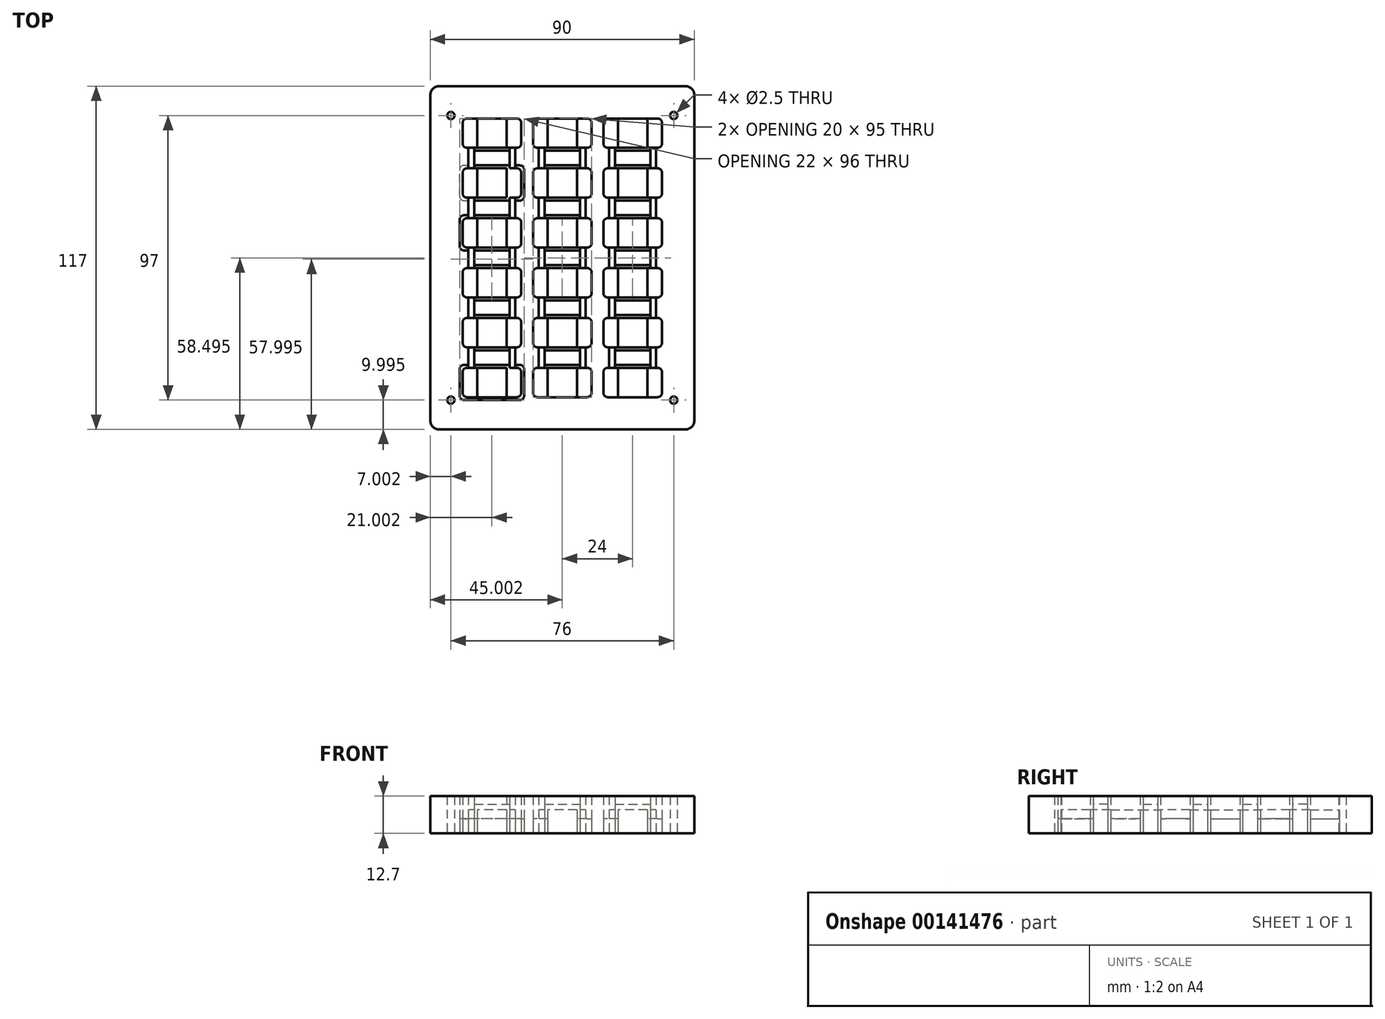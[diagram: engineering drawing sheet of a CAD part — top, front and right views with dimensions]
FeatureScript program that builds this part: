
annotation { "Feature Type Name" : "Feature", "Feature Type Description" : "" }
export const myFeature = defineFeature(function(context is Context, id is Id, definition is map)
    precondition{}
    {
        {
            var Q0;
            Q0=qCreatedBy(makeId("Top.planeOp"),FACE);
            var sketch = newSketch(context, id + "F0", { "sketchPlane" : qUnion([Q0])});
            skPoint(sketch, "E0.middle", {"position": v(0.2, -0.97) * mm});
            skArc(sketch, "E1.MirrorCS", {"start": v(-14.92, -36.63) * mm, "mid": v(-13.86, -37.07) * mm, "end": v(-13.42, -38.13) * mm});
            skLineSegment(sketch, "E2.MirrorCS", {"start": v(-31.42, -33.13) * mm, "end": v(-31.42, -36.63) * mm});
            skLineSegment(sketch, "E3.MirrorCS", {"start": v(-29.42, -33.13) * mm, "end": v(-29.42, -36.63) * mm});
            skArc(sketch, "E4.MirrorCS", {"start": v(-13.42, -45.13) * mm, "mid": v(-13.86, -46.2) * mm, "end": v(-14.92, -46.63) * mm});
            skArc(sketch, "E5.MirrorCS", {"start": v(-33.42, -38.13) * mm, "mid": v(-32.98, -37.07) * mm, "end": v(-31.92, -36.63) * mm});
            skArc(sketch, "E6.MirrorCS", {"start": v(-31.92, -46.63) * mm, "mid": v(-32.98, -46.2) * mm, "end": v(-33.42, -45.13) * mm});
            skLineSegment(sketch, "E7.MirrorCS", {"start": v(-13.42, -38.13) * mm, "end": v(-13.42, -45.13) * mm});
            skLineSegment(sketch, "E8.MirrorCS", {"start": v(-14.92, -36.63) * mm, "end": v(-31.92, -36.63) * mm});
            skLineSegment(sketch, "E9.MirrorCS", {"start": v(-14.92, -46.63) * mm, "end": v(-31.92, -46.63) * mm});
            skLineSegment(sketch, "E10.MirrorCS", {"start": v(-33.42, -38.13) * mm, "end": v(-33.42, -45.13) * mm});
            skPoint(sketch, "E11.MirrorP", {"position": v(-33.42, -47.63) * mm});
            skLineSegment(sketch, "E12.MirrorCS", {"start": v(-28.42, -46.63) * mm, "end": v(-28.42, -36.63) * mm});
            skPoint(sketch, "E13.MirrorP", {"position": v(-13.42, -37.63) * mm});
            skPoint(sketch, "E14.MirrorP", {"position": v(-33.42, -37.63) * mm});
            skPoint(sketch, "E15.MirrorP", {"position": v(-13.42, -47.63) * mm});
            skLineSegment(sketch, "E16.bottom", {"start": v(-13.92, -47.63) * mm, "end": v(-32.92, -47.63) * mm});
            skLineSegment(sketch, "E16.left", {"start": v(-12.42, -46.13) * mm, "end": v(-12.42, -37.13) * mm});
            skLineSegment(sketch, "E16.right", {"start": v(-34.42, -46.13) * mm, "end": v(-34.42, -37.13) * mm});
            skPoint(sketch, "E16.middle", {"position": v(-23.42, -41.63) * mm});
            skArc(sketch, "E17.filletArc", {"start": v(-13.92, -47.63) * mm, "mid": v(-12.86, -47.2) * mm, "end": v(-12.42, -46.13) * mm});
            skPoint(sketch, "E18.visualSharp", {"position": v(-34.42, -47.63) * mm});
            skArc(sketch, "E18.filletArc", {"start": v(-34.42, -46.13) * mm, "mid": v(-33.98, -47.2) * mm, "end": v(-32.92, -47.63) * mm});
            skPoint(sketch, "E19.visualSharp", {"position": v(-34.42, -35.63) * mm});
            skArc(sketch, "E19.filletArc", {"start": v(-32.92, -35.63) * mm, "mid": v(-33.98, -36.07) * mm, "end": v(-34.42, -37.13) * mm});
            skArc(sketch, "E20.filletArc", {"start": v(-12.42, -37.13) * mm, "mid": v(-12.86, -36.07) * mm, "end": v(-13.92, -35.63) * mm});
            skLineSegment(sketch, "E21", {"start": v(-32.92, -35.63) * mm, "end": v(-31.42, -35.63) * mm});
            skLineSegment(sketch, "E22", {"start": v(-29.42, -35.63) * mm, "end": v(-17.42, -35.63) * mm});
            skLineSegment(sketch, "E23", {"start": v(-13.92, -35.63) * mm, "end": v(-15.42, -35.63) * mm});
            skLineSegment(sketch, "E24", {"start": v(-15.42, -36.63) * mm, "end": v(-15.42, -33.13) * mm});
            skLineSegment(sketch, "E25", {"start": v(-17.42, -36.63) * mm, "end": v(-17.42, -33.13) * mm});
            skLineSegment(sketch, "E26", {"start": v(-18.42, -36.63) * mm, "end": v(-18.42, -46.63) * mm});
            skArc(sketch, "E27.MirrorCS", {"start": v(-31.92, -19.63) * mm, "mid": v(-32.98, -20.07) * mm, "end": v(-33.42, -21.13) * mm});
            skPoint(sketch, "E28.MirrorP", {"position": v(-34.42, -30.63) * mm});
            skPoint(sketch, "E29.MirrorP", {"position": v(-23.42, -24.63) * mm});
            skLineSegment(sketch, "E30.MirrorCS", {"start": v(-14.92, -29.63) * mm, "end": v(-31.92, -29.63) * mm});
            skLineSegment(sketch, "E31.MirrorCS", {"start": v(-29.42, -30.63) * mm, "end": v(-17.42, -30.63) * mm});
            skLineSegment(sketch, "E32.MirrorCS", {"start": v(-13.42, -28.13) * mm, "end": v(-13.42, -21.13) * mm});
            skPoint(sketch, "E33.MirrorP", {"position": v(-34.42, -18.63) * mm});
            skArc(sketch, "E34.MirrorCS", {"start": v(-14.92, -29.63) * mm, "mid": v(-13.86, -29.2) * mm, "end": v(-13.42, -28.13) * mm});
            skPoint(sketch, "E35.MirrorP", {"position": v(-13.42, -18.63) * mm});
            skArc(sketch, "E36.MirrorCS", {"start": v(-34.42, -20.13) * mm, "mid": v(-33.98, -19.07) * mm, "end": v(-32.92, -18.63) * mm});
            skLineSegment(sketch, "E37.MirrorCS", {"start": v(-33.42, -28.13) * mm, "end": v(-33.42, -21.13) * mm});
            skLineSegment(sketch, "E38.MirrorCS", {"start": v(-14.92, -19.63) * mm, "end": v(-31.92, -19.63) * mm});
            skArc(sketch, "E39.MirrorCS", {"start": v(-13.42, -21.13) * mm, "mid": v(-13.86, -20.07) * mm, "end": v(-14.92, -19.63) * mm});
            skLineSegment(sketch, "E40.MirrorCS", {"start": v(-12.42, -20.13) * mm, "end": v(-12.42, -29.13) * mm});
            skPoint(sketch, "E41.MirrorP", {"position": v(-13.42, -28.63) * mm});
            skPoint(sketch, "E42.MirrorP", {"position": v(-33.42, -18.63) * mm});
            skLineSegment(sketch, "E43.MirrorCS", {"start": v(-13.92, -30.63) * mm, "end": v(-15.42, -30.63) * mm});
            skLineSegment(sketch, "E44.MirrorCS", {"start": v(-29.42, -33.13) * mm, "end": v(-29.42, -29.63) * mm});
            skArc(sketch, "E45.MirrorCS", {"start": v(-33.42, -28.13) * mm, "mid": v(-32.98, -29.2) * mm, "end": v(-31.92, -29.63) * mm});
            skLineSegment(sketch, "E46.MirrorCS", {"start": v(-28.42, -19.63) * mm, "end": v(-28.42, -29.63) * mm});
            skLineSegment(sketch, "E47.MirrorCS", {"start": v(-34.42, -20.13) * mm, "end": v(-34.42, -29.13) * mm});
            skLineSegment(sketch, "E48.MirrorCS", {"start": v(-15.42, -29.63) * mm, "end": v(-15.42, -33.13) * mm});
            skArc(sketch, "E49.MirrorCS", {"start": v(-13.92, -18.63) * mm, "mid": v(-12.86, -19.07) * mm, "end": v(-12.42, -20.13) * mm});
            skLineSegment(sketch, "E50.MirrorCS", {"start": v(-17.42, -29.63) * mm, "end": v(-17.42, -33.13) * mm});
            skPoint(sketch, "E51.MirrorP", {"position": v(-33.42, -28.63) * mm});
            skLineSegment(sketch, "E52.MirrorCS", {"start": v(-31.42, -33.13) * mm, "end": v(-31.42, -29.63) * mm});
            skArc(sketch, "E53.MirrorCS", {"start": v(-12.42, -29.13) * mm, "mid": v(-12.86, -30.2) * mm, "end": v(-13.92, -30.63) * mm});
            skArc(sketch, "E54.MirrorCS", {"start": v(-32.92, -30.63) * mm, "mid": v(-33.98, -30.2) * mm, "end": v(-34.42, -29.13) * mm});
            skLineSegment(sketch, "E55.MirrorCS", {"start": v(-32.92, -30.63) * mm, "end": v(-31.42, -30.63) * mm});
            skLineSegment(sketch, "E56.MirrorCS", {"start": v(-18.42, -29.63) * mm, "end": v(-18.42, -19.63) * mm});
            skLineSegment(sketch, "E57", {"start": v(-29.42, -19.63) * mm, "end": v(-29.42, -16.13) * mm});
            skLineSegment(sketch, "E58", {"start": v(-31.42, -19.63) * mm, "end": v(-31.42, -16.13) * mm});
            skLineSegment(sketch, "E59", {"start": v(-17.42, -19.63) * mm, "end": v(-17.42, -16.13) * mm});
            skLineSegment(sketch, "E60", {"start": v(-15.42, -19.63) * mm, "end": v(-15.42, -16.13) * mm});
            skLineSegment(sketch, "E61.MirrorCS", {"start": v(-33.42, -4.13) * mm, "end": v(-33.42, -11.13) * mm});
            skArc(sketch, "E62.MirrorCS", {"start": v(-31.92, -12.63) * mm, "mid": v(-32.98, -12.2) * mm, "end": v(-33.42, -11.13) * mm});
            skPoint(sketch, "E63.MirrorP", {"position": v(-13.42, -3.63) * mm});
            skLineSegment(sketch, "E64.MirrorCS", {"start": v(-17.42, -2.63) * mm, "end": v(-17.42, 0.87) * mm});
            skLineSegment(sketch, "E65.MirrorCS", {"start": v(-32.92, -1.63) * mm, "end": v(-31.42, -1.63) * mm});
            skPoint(sketch, "E66.MirrorP", {"position": v(-13.42, -13.63) * mm});
            skArc(sketch, "E67.MirrorCS", {"start": v(-13.92, -13.63) * mm, "mid": v(-12.86, -13.2) * mm, "end": v(-12.42, -12.13) * mm});
            skLineSegment(sketch, "E68.MirrorCS", {"start": v(-17.42, -12.63) * mm, "end": v(-17.42, -16.13) * mm});
            skLineSegment(sketch, "E69.MirrorCS", {"start": v(-15.42, -12.63) * mm, "end": v(-15.42, -16.13) * mm});
            skLineSegment(sketch, "E70.MirrorCS", {"start": v(-31.42, 0.87) * mm, "end": v(-31.42, -2.63) * mm});
            skLineSegment(sketch, "E71.MirrorCS", {"start": v(-13.42, -4.13) * mm, "end": v(-13.42, -11.13) * mm});
            skLineSegment(sketch, "E72.MirrorCS", {"start": v(-29.42, -12.63) * mm, "end": v(-29.42, -16.13) * mm});
            skLineSegment(sketch, "E73.MirrorCS", {"start": v(-15.42, -2.63) * mm, "end": v(-15.42, 0.87) * mm});
            skLineSegment(sketch, "E74.MirrorCS", {"start": v(-12.42, -12.13) * mm, "end": v(-12.42, -3.13) * mm});
            skArc(sketch, "E75.MirrorCS", {"start": v(-13.42, -11.13) * mm, "mid": v(-13.86, -12.2) * mm, "end": v(-14.92, -12.63) * mm});
            skLineSegment(sketch, "E76.MirrorCS", {"start": v(-29.42, -1.63) * mm, "end": v(-17.42, -1.63) * mm});
            skLineSegment(sketch, "E77.MirrorCS", {"start": v(-29.42, 0.87) * mm, "end": v(-29.42, -2.63) * mm});
            skLineSegment(sketch, "E78.MirrorCS", {"start": v(-13.92, -1.63) * mm, "end": v(-15.42, -1.63) * mm});
            skArc(sketch, "E79.MirrorCS", {"start": v(-33.42, -4.13) * mm, "mid": v(-32.98, -3.07) * mm, "end": v(-31.92, -2.63) * mm});
            skPoint(sketch, "E80.MirrorP", {"position": v(-33.42, -13.63) * mm});
            skArc(sketch, "E81.MirrorCS", {"start": v(-14.92, -2.63) * mm, "mid": v(-13.86, -3.07) * mm, "end": v(-13.42, -4.13) * mm});
            skLineSegment(sketch, "E82.MirrorCS", {"start": v(-14.92, -2.63) * mm, "end": v(-31.92, -2.63) * mm});
            skPoint(sketch, "E83.MirrorP", {"position": v(-34.42, -1.63) * mm});
            skLineSegment(sketch, "E84.MirrorCS", {"start": v(-14.92, -12.63) * mm, "end": v(-31.92, -12.63) * mm});
            skPoint(sketch, "E85.MirrorP", {"position": v(-34.42, -13.63) * mm});
            skArc(sketch, "E86.MirrorCS", {"start": v(-12.42, -3.13) * mm, "mid": v(-12.86, -2.07) * mm, "end": v(-13.92, -1.63) * mm});
            skLineSegment(sketch, "E87.MirrorCS", {"start": v(-18.42, -2.63) * mm, "end": v(-18.42, -12.63) * mm});
            skArc(sketch, "E88.MirrorCS", {"start": v(-34.42, -12.13) * mm, "mid": v(-33.98, -13.2) * mm, "end": v(-32.92, -13.63) * mm});
            skLineSegment(sketch, "E89.MirrorCS", {"start": v(-34.42, -12.13) * mm, "end": v(-34.42, -3.13) * mm});
            skArc(sketch, "E90.MirrorCS", {"start": v(-32.92, -1.63) * mm, "mid": v(-33.98, -2.07) * mm, "end": v(-34.42, -3.13) * mm});
            skPoint(sketch, "E91.MirrorP", {"position": v(-33.42, -3.63) * mm});
            skLineSegment(sketch, "E92.MirrorCS", {"start": v(-28.42, -12.63) * mm, "end": v(-28.42, -2.63) * mm});
            skPoint(sketch, "E93.MirrorP", {"position": v(-23.42, -7.63) * mm});
            skLineSegment(sketch, "E94.MirrorCS", {"start": v(-31.42, -12.63) * mm, "end": v(-31.42, -16.13) * mm});
            skArc(sketch, "E95.MirrorCS", {"start": v(-32.92, 3.37) * mm, "mid": v(-33.98, 3.8) * mm, "end": v(-34.42, 4.87) * mm});
            skArc(sketch, "E96.MirrorCS", {"start": v(-33.42, 5.87) * mm, "mid": v(-32.98, 4.8) * mm, "end": v(-31.92, 4.37) * mm});
            skArc(sketch, "E97.MirrorCS", {"start": v(-14.92, 4.37) * mm, "mid": v(-13.86, 4.8) * mm, "end": v(-13.42, 5.87) * mm});
            skArc(sketch, "E98.MirrorCS", {"start": v(-12.42, 4.87) * mm, "mid": v(-12.86, 3.8) * mm, "end": v(-13.92, 3.37) * mm});
            skArc(sketch, "E99.MirrorCS", {"start": v(-13.42, 12.87) * mm, "mid": v(-13.86, 13.93) * mm, "end": v(-14.92, 14.37) * mm});
            skArc(sketch, "E100.MirrorCS", {"start": v(-31.92, 14.37) * mm, "mid": v(-32.98, 13.93) * mm, "end": v(-33.42, 12.87) * mm});
            skArc(sketch, "E101.MirrorCS", {"start": v(-13.92, 15.37) * mm, "mid": v(-12.86, 14.93) * mm, "end": v(-12.42, 13.87) * mm});
            skArc(sketch, "E102.MirrorCS", {"start": v(-34.42, 13.87) * mm, "mid": v(-33.98, 14.93) * mm, "end": v(-32.92, 15.37) * mm});
            skLineSegment(sketch, "E103.MirrorCS", {"start": v(-15.42, 4.37) * mm, "end": v(-15.42, 0.87) * mm});
            skLineSegment(sketch, "E104.MirrorCS", {"start": v(-32.92, 3.37) * mm, "end": v(-31.42, 3.37) * mm});
            skLineSegment(sketch, "E105.MirrorCS", {"start": v(-17.42, 4.37) * mm, "end": v(-17.42, 0.87) * mm});
            skLineSegment(sketch, "E106.MirrorCS", {"start": v(-13.92, 3.37) * mm, "end": v(-15.42, 3.37) * mm});
            skLineSegment(sketch, "E107.MirrorCS", {"start": v(-29.42, 0.87) * mm, "end": v(-29.42, 4.37) * mm});
            skLineSegment(sketch, "E108.MirrorCS", {"start": v(-31.42, 0.87) * mm, "end": v(-31.42, 4.37) * mm});
            skPoint(sketch, "E109.MirrorP", {"position": v(-34.42, 3.37) * mm});
            skPoint(sketch, "E110.MirrorP", {"position": v(-33.42, 5.37) * mm});
            skPoint(sketch, "E111.MirrorP", {"position": v(-34.42, 15.37) * mm});
            skLineSegment(sketch, "E112.MirrorCS", {"start": v(-29.42, 3.37) * mm, "end": v(-17.42, 3.37) * mm});
            skLineSegment(sketch, "E113.MirrorCS", {"start": v(-14.92, 14.37) * mm, "end": v(-31.92, 14.37) * mm});
            skPoint(sketch, "E114.MirrorP", {"position": v(-23.42, 9.37) * mm});
            skLineSegment(sketch, "E115.MirrorCS", {"start": v(-12.42, 13.87) * mm, "end": v(-12.42, 4.87) * mm});
            skLineSegment(sketch, "E116.MirrorCS", {"start": v(-28.42, 14.37) * mm, "end": v(-28.42, 4.37) * mm});
            skLineSegment(sketch, "E117.MirrorCS", {"start": v(-17.42, 14.37) * mm, "end": v(-17.42, 17.87) * mm});
            skLineSegment(sketch, "E118.MirrorCS", {"start": v(-14.92, 4.37) * mm, "end": v(-31.92, 4.37) * mm});
            skLineSegment(sketch, "E119.MirrorCS", {"start": v(-33.42, 5.87) * mm, "end": v(-33.42, 12.87) * mm});
            skLineSegment(sketch, "E120.MirrorCS", {"start": v(-13.42, 5.87) * mm, "end": v(-13.42, 12.87) * mm});
            skLineSegment(sketch, "E121.MirrorCS", {"start": v(-34.42, 13.87) * mm, "end": v(-34.42, 4.87) * mm});
            skPoint(sketch, "E122.MirrorP", {"position": v(-13.42, 5.37) * mm});
            skPoint(sketch, "E123.MirrorP", {"position": v(-33.42, 15.37) * mm});
            skLineSegment(sketch, "E124.MirrorCS", {"start": v(-31.42, 14.37) * mm, "end": v(-31.42, 17.87) * mm});
            skLineSegment(sketch, "E125.MirrorCS", {"start": v(-18.42, 4.37) * mm, "end": v(-18.42, 14.37) * mm});
            skLineSegment(sketch, "E126.MirrorCS", {"start": v(-15.42, 14.37) * mm, "end": v(-15.42, 17.87) * mm});
            skPoint(sketch, "E127.MirrorP", {"position": v(-13.42, 15.37) * mm});
            skLineSegment(sketch, "E128.MirrorCS", {"start": v(-29.42, 14.37) * mm, "end": v(-29.42, 17.87) * mm});
            skArc(sketch, "E129.MirrorCS", {"start": v(-13.42, 22.87) * mm, "mid": v(-13.86, 21.8) * mm, "end": v(-14.92, 21.37) * mm});
            skLineSegment(sketch, "E130.MirrorCS", {"start": v(-32.92, 32.37) * mm, "end": v(-31.42, 32.37) * mm});
            skArc(sketch, "E131.MirrorCS", {"start": v(-13.92, 20.37) * mm, "mid": v(-12.86, 20.8) * mm, "end": v(-12.42, 21.87) * mm});
            skArc(sketch, "E132.MirrorCS", {"start": v(-12.42, 30.87) * mm, "mid": v(-12.86, 31.93) * mm, "end": v(-13.92, 32.37) * mm});
            skArc(sketch, "E133.MirrorCS", {"start": v(-14.92, 31.37) * mm, "mid": v(-13.86, 30.93) * mm, "end": v(-13.42, 29.87) * mm});
            skLineSegment(sketch, "E134.MirrorCS", {"start": v(-13.92, 32.37) * mm, "end": v(-15.42, 32.37) * mm});
            skArc(sketch, "E135.MirrorCS", {"start": v(-32.92, 32.37) * mm, "mid": v(-33.98, 31.93) * mm, "end": v(-34.42, 30.87) * mm});
            skArc(sketch, "E136.MirrorCS", {"start": v(-31.92, 21.37) * mm, "mid": v(-32.98, 21.8) * mm, "end": v(-33.42, 22.87) * mm});
            skArc(sketch, "E137.MirrorCS", {"start": v(-33.42, 29.87) * mm, "mid": v(-32.98, 30.93) * mm, "end": v(-31.92, 31.37) * mm});
            skArc(sketch, "E138.MirrorCS", {"start": v(-34.42, 21.87) * mm, "mid": v(-33.98, 20.8) * mm, "end": v(-32.92, 20.37) * mm});
            skLineSegment(sketch, "E139.MirrorCS", {"start": v(-17.42, 31.37) * mm, "end": v(-17.42, 34.87) * mm});
            skLineSegment(sketch, "E140.MirrorCS", {"start": v(-15.42, 21.37) * mm, "end": v(-15.42, 17.87) * mm});
            skLineSegment(sketch, "E141.MirrorCS", {"start": v(-14.92, 31.37) * mm, "end": v(-31.92, 31.37) * mm});
            skPoint(sketch, "E142.MirrorP", {"position": v(-23.42, 26.37) * mm});
            skPoint(sketch, "E143.MirrorP", {"position": v(-33.42, 30.37) * mm});
            skLineSegment(sketch, "E144.MirrorCS", {"start": v(-17.42, 21.37) * mm, "end": v(-17.42, 17.87) * mm});
            skLineSegment(sketch, "E145.MirrorCS", {"start": v(-14.92, 21.37) * mm, "end": v(-31.92, 21.37) * mm});
            skLineSegment(sketch, "E146.MirrorCS", {"start": v(-28.42, 21.37) * mm, "end": v(-28.42, 31.37) * mm});
            skPoint(sketch, "E147.MirrorP", {"position": v(-34.42, 32.37) * mm});
            skLineSegment(sketch, "E148.MirrorCS", {"start": v(-29.42, 21.37) * mm, "end": v(-29.42, 17.87) * mm});
            skPoint(sketch, "E149.MirrorP", {"position": v(-34.42, 20.37) * mm});
            skPoint(sketch, "E150.MirrorP", {"position": v(-13.42, 30.37) * mm});
            skLineSegment(sketch, "E151.MirrorCS", {"start": v(-18.42, 31.37) * mm, "end": v(-18.42, 21.37) * mm});
            skLineSegment(sketch, "E152.MirrorCS", {"start": v(-29.42, 34.87) * mm, "end": v(-29.42, 31.37) * mm});
            skLineSegment(sketch, "E153.MirrorCS", {"start": v(-31.42, 34.87) * mm, "end": v(-31.42, 31.37) * mm});
            skLineSegment(sketch, "E154.MirrorCS", {"start": v(-34.42, 21.87) * mm, "end": v(-34.42, 30.87) * mm});
            skPoint(sketch, "E155.MirrorP", {"position": v(-13.42, 20.37) * mm});
            skLineSegment(sketch, "E156.MirrorCS", {"start": v(-12.42, 21.87) * mm, "end": v(-12.42, 30.87) * mm});
            skPoint(sketch, "E157.MirrorP", {"position": v(-33.42, 20.37) * mm});
            skLineSegment(sketch, "E158.MirrorCS", {"start": v(-31.42, 21.37) * mm, "end": v(-31.42, 17.87) * mm});
            skLineSegment(sketch, "E159.MirrorCS", {"start": v(-33.42, 29.87) * mm, "end": v(-33.42, 22.87) * mm});
            skLineSegment(sketch, "E160.MirrorCS", {"start": v(-15.42, 31.37) * mm, "end": v(-15.42, 34.87) * mm});
            skLineSegment(sketch, "E161.MirrorCS", {"start": v(-13.42, 29.87) * mm, "end": v(-13.42, 22.87) * mm});
            skLineSegment(sketch, "E162.MirrorCS", {"start": v(-29.42, 32.37) * mm, "end": v(-17.42, 32.37) * mm});
            skArc(sketch, "E163.MirrorCS", {"start": v(-13.42, 46.87) * mm, "mid": v(-13.86, 47.93) * mm, "end": v(-14.92, 48.37) * mm});
            skArc(sketch, "E164.MirrorCS", {"start": v(-32.92, 37.37) * mm, "mid": v(-33.98, 37.8) * mm, "end": v(-34.42, 38.87) * mm});
            skArc(sketch, "E165.MirrorCS", {"start": v(-34.42, 47.87) * mm, "mid": v(-33.98, 48.93) * mm, "end": v(-32.92, 49.37) * mm});
            skArc(sketch, "E166.MirrorCS", {"start": v(-33.42, 39.87) * mm, "mid": v(-32.98, 38.8) * mm, "end": v(-31.92, 38.37) * mm});
            skArc(sketch, "E167.MirrorCS", {"start": v(-14.92, 38.37) * mm, "mid": v(-13.86, 38.8) * mm, "end": v(-13.42, 39.87) * mm});
            skArc(sketch, "E168.MirrorCS", {"start": v(-12.42, 38.87) * mm, "mid": v(-12.86, 37.8) * mm, "end": v(-13.92, 37.37) * mm});
            skArc(sketch, "E169.MirrorCS", {"start": v(-31.92, 48.37) * mm, "mid": v(-32.98, 47.93) * mm, "end": v(-33.42, 46.87) * mm});
            skArc(sketch, "E170.MirrorCS", {"start": v(-13.92, 49.37) * mm, "mid": v(-12.86, 48.93) * mm, "end": v(-12.42, 47.87) * mm});
            skLineSegment(sketch, "E171.MirrorCS", {"start": v(-13.92, 37.37) * mm, "end": v(-15.42, 37.37) * mm});
            skLineSegment(sketch, "E172.MirrorCS", {"start": v(-15.42, 38.37) * mm, "end": v(-15.42, 34.87) * mm});
            skLineSegment(sketch, "E173.MirrorCS", {"start": v(-18.42, 38.37) * mm, "end": v(-18.42, 48.37) * mm});
            skLineSegment(sketch, "E174.MirrorCS", {"start": v(-13.42, 39.87) * mm, "end": v(-13.42, 46.87) * mm});
            skLineSegment(sketch, "E175.MirrorCS", {"start": v(-32.92, 37.37) * mm, "end": v(-31.42, 37.37) * mm});
            skLineSegment(sketch, "E176.MirrorCS", {"start": v(-12.42, 47.87) * mm, "end": v(-12.42, 38.87) * mm});
            skLineSegment(sketch, "E177.MirrorCS", {"start": v(-13.92, 49.37) * mm, "end": v(-32.92, 49.37) * mm});
            skLineSegment(sketch, "E178.MirrorCS", {"start": v(-17.42, 38.37) * mm, "end": v(-17.42, 34.87) * mm});
            skLineSegment(sketch, "E179.MirrorCS", {"start": v(-28.42, 48.37) * mm, "end": v(-28.42, 38.37) * mm});
            skLineSegment(sketch, "E180.MirrorCS", {"start": v(-33.42, 39.87) * mm, "end": v(-33.42, 46.87) * mm});
            skPoint(sketch, "E181.MirrorP", {"position": v(-13.42, 39.37) * mm});
            skLineSegment(sketch, "E182.MirrorCS", {"start": v(-31.42, 34.87) * mm, "end": v(-31.42, 38.37) * mm});
            skPoint(sketch, "E183.MirrorP", {"position": v(-33.42, 39.37) * mm});
            skLineSegment(sketch, "E184.MirrorCS", {"start": v(-29.42, 37.37) * mm, "end": v(-17.42, 37.37) * mm});
            skPoint(sketch, "E185.MirrorP", {"position": v(-23.42, 43.37) * mm});
            skLineSegment(sketch, "E186.MirrorCS", {"start": v(-34.42, 47.87) * mm, "end": v(-34.42, 38.87) * mm});
            skLineSegment(sketch, "E187.MirrorCS", {"start": v(-29.42, 34.87) * mm, "end": v(-29.42, 38.37) * mm});
            skLineSegment(sketch, "E188.MirrorCS", {"start": v(-14.92, 38.37) * mm, "end": v(-31.92, 38.37) * mm});
            skPoint(sketch, "E189.MirrorP", {"position": v(-34.42, 37.37) * mm});
            skLineSegment(sketch, "E190.MirrorCS", {"start": v(-14.92, 48.37) * mm, "end": v(-31.92, 48.37) * mm});
            skLineSegment(sketch, "E191", {"start": v(-32.92, -13.63) * mm, "end": v(-31.42, -13.63) * mm});
            skLineSegment(sketch, "E192", {"start": v(-13.92, -13.63) * mm, "end": v(-15.42, -13.63) * mm});
            skLineSegment(sketch, "E193", {"start": v(-13.92, -18.63) * mm, "end": v(-15.42, -18.63) * mm});
            skLineSegment(sketch, "E194", {"start": v(-32.92, -18.63) * mm, "end": v(-31.42, -18.63) * mm});
            skLineSegment(sketch, "E195", {"start": v(-32.92, 20.37) * mm, "end": v(-31.42, 20.37) * mm});
            skLineSegment(sketch, "E196", {"start": v(-13.92, 20.37) * mm, "end": v(-15.42, 20.37) * mm});
            skLineSegment(sketch, "E197", {"start": v(-32.92, 15.37) * mm, "end": v(-31.42, 15.37) * mm});
            skLineSegment(sketch, "E198", {"start": v(-13.92, 15.37) * mm, "end": v(-15.42, 15.37) * mm});
            skLineSegment(sketch, "E199", {"start": v(-29.42, -13.63) * mm, "end": v(-17.42, -13.63) * mm});
            skPoint(sketch, "E199.startSnap0", {"position": v(-29.42, -14.38) * mm});
            skLineSegment(sketch, "E200", {"start": v(-29.42, 20.37) * mm, "end": v(-17.42, 20.37) * mm});
            skLineSegment(sketch, "E201", {"start": v(-29.42, 15.37) * mm, "end": v(-17.42, 15.37) * mm});
            skPoint(sketch, "E201.endSnap0", {"position": v(-17.42, 16.12) * mm});
            skLineSegment(sketch, "E202", {"start": v(-29.42, -18.63) * mm, "end": v(-17.42, -18.63) * mm});
            skPoint(sketch, "E202.endSnap0", {"position": v(-17.42, -17.88) * mm});
            skPoint(sketch, "E203.1.0.0", {"position": v(10.58, -18.63) * mm});
            skPoint(sketch, "E203.1.0.1", {"position": v(0.58, 26.37) * mm});
            skPoint(sketch, "E203.1.0.2", {"position": v(-9.42, -47.63) * mm});
            skPoint(sketch, "E203.1.0.3", {"position": v(-9.42, 39.37) * mm});
            skLineSegment(sketch, "E203.1.0.4", {"start": v(-4.42, 48.37) * mm, "end": v(-4.42, 38.37) * mm});
            skLineSegment(sketch, "E203.1.0.5", {"start": v(-5.42, -13.63) * mm, "end": v(6.58, -13.63) * mm});
            skPoint(sketch, "E203.1.0.6", {"position": v(-10.42, 3.37) * mm});
            skPoint(sketch, "E203.1.0.7", {"position": v(10.58, -37.63) * mm});
            skPoint(sketch, "E203.1.0.8", {"position": v(-9.42, 30.37) * mm});
            skPoint(sketch, "E203.1.0.9", {"position": v(0.58, 43.37) * mm});
            skLineSegment(sketch, "E203.1.0.10", {"start": v(9.08, -2.63) * mm, "end": v(-7.92, -2.63) * mm});
            skLineSegment(sketch, "E203.1.0.11", {"start": v(-4.42, -19.63) * mm, "end": v(-4.42, -29.63) * mm});
            skLineSegment(sketch, "E203.1.0.12", {"start": v(9.08, 31.37) * mm, "end": v(-7.92, 31.37) * mm});
            skLineSegment(sketch, "E203.1.0.13", {"start": v(-5.42, 20.37) * mm, "end": v(6.58, 20.37) * mm});
            skPoint(sketch, "E203.1.0.14", {"position": v(-9.42, 5.37) * mm});
            skPoint(sketch, "E203.1.0.15", {"position": v(-10.42, -1.63) * mm});
            skPoint(sketch, "E203.1.0.16", {"position": v(-9.42, -37.63) * mm});
            skPoint(sketch, "E203.1.0.17", {"position": v(-10.42, 32.37) * mm});
            skPoint(sketch, "E203.1.0.18", {"position": v(-10.42, 37.37) * mm});
            skLineSegment(sketch, "E203.1.0.19", {"start": v(9.08, -12.63) * mm, "end": v(-7.92, -12.63) * mm});
            skLineSegment(sketch, "E203.1.0.20", {"start": v(5.58, 4.37) * mm, "end": v(5.58, 14.37) * mm});
            skLineSegment(sketch, "E203.1.0.21", {"start": v(-5.42, 15.37) * mm, "end": v(6.58, 15.37) * mm});
            skPoint(sketch, "E203.1.0.22", {"position": v(10.58, -28.63) * mm});
            skPoint(sketch, "E203.1.0.23", {"position": v(10.58, -47.63) * mm});
            skPoint(sketch, "E203.1.0.24", {"position": v(-10.42, 15.37) * mm});
            skPoint(sketch, "E203.1.0.25", {"position": v(-10.42, 20.37) * mm});
            skPoint(sketch, "E203.1.0.26", {"position": v(-10.42, -13.63) * mm});
            skLineSegment(sketch, "E203.1.0.27", {"start": v(5.58, -36.63) * mm, "end": v(5.58, -46.63) * mm});
            skPoint(sketch, "E203.1.0.28", {"position": v(-5.42, -14.38) * mm});
            skLineSegment(sketch, "E203.1.0.29", {"start": v(9.08, 21.37) * mm, "end": v(-7.92, 21.37) * mm});
            skLineSegment(sketch, "E203.1.0.30", {"start": v(-5.42, -18.63) * mm, "end": v(6.58, -18.63) * mm});
            skLineSegment(sketch, "E203.1.0.31", {"start": v(-5.42, 37.37) * mm, "end": v(6.58, 37.37) * mm});
            skPoint(sketch, "E203.1.0.32", {"position": v(-9.42, -18.63) * mm});
            skPoint(sketch, "E203.1.0.33", {"position": v(0.58, -41.63) * mm});
            skPoint(sketch, "E203.1.0.34", {"position": v(10.58, 30.37) * mm});
            skPoint(sketch, "E203.1.0.35", {"position": v(0.58, 9.37) * mm});
            skPoint(sketch, "E203.1.0.36", {"position": v(6.58, 16.12) * mm});
            skLineSegment(sketch, "E203.1.0.37", {"start": v(-4.42, 21.37) * mm, "end": v(-4.42, 31.37) * mm});
            skLineSegment(sketch, "E203.1.0.38", {"start": v(5.58, -2.63) * mm, "end": v(5.58, -12.63) * mm});
            skPoint(sketch, "E203.1.0.39", {"position": v(10.58, 20.37) * mm});
            skPoint(sketch, "E203.1.0.40", {"position": v(10.58, 5.37) * mm});
            skLineSegment(sketch, "E203.1.0.41", {"start": v(9.08, -29.63) * mm, "end": v(-7.92, -29.63) * mm});
            skPoint(sketch, "E203.1.0.42", {"position": v(6.58, -17.88) * mm});
            skPoint(sketch, "E203.1.0.43", {"position": v(-10.42, -47.63) * mm});
            skPoint(sketch, "E203.1.0.44", {"position": v(-9.42, 15.37) * mm});
            skPoint(sketch, "E203.1.0.45", {"position": v(-9.42, 20.37) * mm});
            skLineSegment(sketch, "E203.1.0.46", {"start": v(-5.42, -30.63) * mm, "end": v(6.58, -30.63) * mm});
            skLineSegment(sketch, "E203.1.0.47", {"start": v(5.58, 31.37) * mm, "end": v(5.58, 21.37) * mm});
            skLineSegment(sketch, "E203.1.0.48", {"start": v(9.08, 38.37) * mm, "end": v(-7.92, 38.37) * mm});
            skPoint(sketch, "E203.1.0.49", {"position": v(-9.42, -3.63) * mm});
            skPoint(sketch, "E203.1.0.50", {"position": v(10.58, 15.37) * mm});
            skLineSegment(sketch, "E203.1.0.51", {"start": v(9.08, 14.37) * mm, "end": v(-7.92, 14.37) * mm});
            skPoint(sketch, "E203.1.0.52", {"position": v(-9.42, -28.63) * mm});
            skLineSegment(sketch, "E203.1.0.53", {"start": v(-5.42, 3.37) * mm, "end": v(6.58, 3.37) * mm});
            skLineSegment(sketch, "E203.1.0.54", {"start": v(-4.42, -12.63) * mm, "end": v(-4.42, -2.63) * mm});
            skLineSegment(sketch, "E203.1.0.55", {"start": v(5.58, -29.63) * mm, "end": v(5.58, -19.63) * mm});
            skLineSegment(sketch, "E203.1.0.56", {"start": v(5.58, 38.37) * mm, "end": v(5.58, 48.37) * mm});
            skPoint(sketch, "E203.1.0.57", {"position": v(-10.42, -35.63) * mm});
            skPoint(sketch, "E203.1.0.58", {"position": v(0.58, -7.63) * mm});
            skPoint(sketch, "E203.1.0.59", {"position": v(10.58, -3.63) * mm});
            skLineSegment(sketch, "E203.1.0.60", {"start": v(9.08, -19.63) * mm, "end": v(-7.92, -19.63) * mm});
            skLineSegment(sketch, "E203.1.0.61", {"start": v(-4.42, 14.37) * mm, "end": v(-4.42, 4.37) * mm});
            skPoint(sketch, "E203.1.0.62", {"position": v(10.58, -13.63) * mm});
            skPoint(sketch, "E203.1.0.63", {"position": v(-10.42, -30.63) * mm});
            skLineSegment(sketch, "E203.1.0.64", {"start": v(-5.42, -1.63) * mm, "end": v(6.58, -1.63) * mm});
            skPoint(sketch, "E203.1.0.65", {"position": v(0.58, -24.63) * mm});
            skLineSegment(sketch, "E203.1.0.66", {"start": v(9.08, 4.37) * mm, "end": v(-7.92, 4.37) * mm});
            skPoint(sketch, "E203.1.0.67", {"position": v(-10.42, -18.63) * mm});
            skLineSegment(sketch, "E203.1.0.68", {"start": v(10.08, 49.37) * mm, "end": v(-8.92, 49.37) * mm});
            skLineSegment(sketch, "E203.1.0.69", {"start": v(-5.42, 32.37) * mm, "end": v(6.58, 32.37) * mm});
            skPoint(sketch, "E203.1.0.70", {"position": v(10.58, 39.37) * mm});
            skPoint(sketch, "E203.1.0.71", {"position": v(-9.42, -13.63) * mm});
            skLineSegment(sketch, "E203.1.0.72", {"start": v(-10.42, -12.13) * mm, "end": v(-10.42, -3.13) * mm});
            skLineSegment(sketch, "E203.1.0.73", {"start": v(10.58, -4.13) * mm, "end": v(10.58, -11.13) * mm});
            skLineSegment(sketch, "E203.1.0.74", {"start": v(9.08, 48.37) * mm, "end": v(-7.92, 48.37) * mm});
            skLineSegment(sketch, "E203.1.0.75", {"start": v(11.58, -12.13) * mm, "end": v(11.58, -3.13) * mm});
            skLineSegment(sketch, "E203.1.0.76", {"start": v(9.08, -36.63) * mm, "end": v(-7.92, -36.63) * mm});
            skLineSegment(sketch, "E203.1.0.77", {"start": v(9.08, -46.63) * mm, "end": v(-7.92, -46.63) * mm});
            skLineSegment(sketch, "E203.1.0.78", {"start": v(-4.42, -46.63) * mm, "end": v(-4.42, -36.63) * mm});
            skLineSegment(sketch, "E203.1.0.79", {"start": v(10.08, -47.63) * mm, "end": v(-8.92, -47.63) * mm});
            skLineSegment(sketch, "E203.1.0.80", {"start": v(-9.42, -4.13) * mm, "end": v(-9.42, -11.13) * mm});
            skLineSegment(sketch, "E203.1.0.81", {"start": v(-5.42, -35.63) * mm, "end": v(6.58, -35.63) * mm});
            skLineSegment(sketch, "E203.1.0.82", {"start": v(-10.42, -20.13) * mm, "end": v(-10.42, -29.13) * mm});
            skLineSegment(sketch, "E203.1.0.83", {"start": v(10.58, -28.13) * mm, "end": v(10.58, -21.13) * mm});
            skLineSegment(sketch, "E203.1.0.84", {"start": v(-10.42, 21.87) * mm, "end": v(-10.42, 30.87) * mm});
            skLineSegment(sketch, "E203.1.0.85", {"start": v(11.58, 21.87) * mm, "end": v(11.58, 30.87) * mm});
            skLineSegment(sketch, "E203.1.0.86", {"start": v(-9.42, -28.13) * mm, "end": v(-9.42, -21.13) * mm});
            skLineSegment(sketch, "E203.1.0.87", {"start": v(-10.42, -46.13) * mm, "end": v(-10.42, -37.13) * mm});
            skLineSegment(sketch, "E203.1.0.88", {"start": v(-9.42, -38.13) * mm, "end": v(-9.42, -45.13) * mm});
            skLineSegment(sketch, "E203.1.0.89", {"start": v(-9.42, 29.87) * mm, "end": v(-9.42, 22.87) * mm});
            skLineSegment(sketch, "E203.1.0.90", {"start": v(11.58, -20.13) * mm, "end": v(11.58, -29.13) * mm});
            skLineSegment(sketch, "E203.1.0.91", {"start": v(10.58, 29.87) * mm, "end": v(10.58, 22.87) * mm});
            skLineSegment(sketch, "E203.1.0.92", {"start": v(-10.42, 13.87) * mm, "end": v(-10.42, 4.87) * mm});
            skLineSegment(sketch, "E203.1.0.93", {"start": v(6.58, -2.63) * mm, "end": v(6.58, 0.87) * mm});
            skLineSegment(sketch, "E203.1.0.94", {"start": v(-9.42, 39.87) * mm, "end": v(-9.42, 46.87) * mm});
            skArc(sketch, "E203.1.0.95", {"start": v(-10.42, 47.87) * mm, "mid": v(-9.98, 48.93) * mm, "end": v(-8.92, 49.37) * mm});
            skLineSegment(sketch, "E203.1.0.96", {"start": v(6.58, 21.37) * mm, "end": v(6.58, 17.87) * mm});
            skLineSegment(sketch, "E203.1.0.97", {"start": v(6.58, 4.37) * mm, "end": v(6.58, 0.87) * mm});
            skLineSegment(sketch, "E203.1.0.98", {"start": v(-10.42, 47.87) * mm, "end": v(-10.42, 38.87) * mm});
            skLineSegment(sketch, "E203.1.0.99", {"start": v(6.58, -29.63) * mm, "end": v(6.58, -33.13) * mm});
            skLineSegment(sketch, "E203.1.0.100", {"start": v(-5.42, 21.37) * mm, "end": v(-5.42, 17.87) * mm});
            skLineSegment(sketch, "E203.1.0.101", {"start": v(-5.42, 34.87) * mm, "end": v(-5.42, 38.37) * mm});
            skLineSegment(sketch, "E203.1.0.102", {"start": v(-5.42, 0.87) * mm, "end": v(-5.42, 4.37) * mm});
            skArc(sketch, "E203.1.0.103", {"start": v(-7.92, 48.37) * mm, "mid": v(-8.98, 47.93) * mm, "end": v(-9.42, 46.87) * mm});
            skArc(sketch, "E203.1.0.104", {"start": v(-8.92, 3.37) * mm, "mid": v(-9.98, 3.8) * mm, "end": v(-10.42, 4.87) * mm});
            skLineSegment(sketch, "E203.1.0.105", {"start": v(11.58, 13.87) * mm, "end": v(11.58, 4.87) * mm});
            skArc(sketch, "E203.1.0.106", {"start": v(-9.42, 5.87) * mm, "mid": v(-8.98, 4.8) * mm, "end": v(-7.92, 4.37) * mm});
            skLineSegment(sketch, "E203.1.0.107", {"start": v(10.58, 39.87) * mm, "end": v(10.58, 46.87) * mm});
            skLineSegment(sketch, "E203.1.0.108", {"start": v(-5.42, -19.63) * mm, "end": v(-5.42, -16.13) * mm});
            skArc(sketch, "E203.1.0.109", {"start": v(10.08, -47.63) * mm, "mid": v(11.14, -47.2) * mm, "end": v(11.58, -46.13) * mm});
            skArc(sketch, "E203.1.0.110", {"start": v(-10.42, -46.13) * mm, "mid": v(-9.98, -47.2) * mm, "end": v(-8.92, -47.63) * mm});
            skArc(sketch, "E203.1.0.111", {"start": v(10.58, -45.13) * mm, "mid": v(10.14, -46.2) * mm, "end": v(9.08, -46.63) * mm});
            skArc(sketch, "E203.1.0.112", {"start": v(-7.92, -46.63) * mm, "mid": v(-8.98, -46.2) * mm, "end": v(-9.42, -45.13) * mm});
            skLineSegment(sketch, "E203.1.0.113", {"start": v(10.58, -38.13) * mm, "end": v(10.58, -45.13) * mm});
            skLineSegment(sketch, "E203.1.0.114", {"start": v(11.58, -46.13) * mm, "end": v(11.58, -37.13) * mm});
            skLineSegment(sketch, "E203.1.0.115", {"start": v(11.58, 47.87) * mm, "end": v(11.58, 38.87) * mm});
            skLineSegment(sketch, "E203.1.0.116", {"start": v(-5.42, 0.87) * mm, "end": v(-5.42, -2.63) * mm});
            skLineSegment(sketch, "E203.1.0.117", {"start": v(-9.42, 5.87) * mm, "end": v(-9.42, 12.87) * mm});
            skLineSegment(sketch, "E203.1.0.118", {"start": v(10.58, 5.87) * mm, "end": v(10.58, 12.87) * mm});
            skArc(sketch, "E203.1.0.119", {"start": v(10.08, 15.37) * mm, "mid": v(11.14, 14.93) * mm, "end": v(11.58, 13.87) * mm});
            skArc(sketch, "E203.1.0.120", {"start": v(-9.42, -28.13) * mm, "mid": v(-8.98, -29.2) * mm, "end": v(-7.92, -29.63) * mm});
            skArc(sketch, "E203.1.0.121", {"start": v(10.58, 46.87) * mm, "mid": v(10.14, 47.93) * mm, "end": v(9.08, 48.37) * mm});
            skLineSegment(sketch, "E203.1.0.122", {"start": v(8.58, 21.37) * mm, "end": v(8.58, 17.87) * mm});
            skArc(sketch, "E203.1.0.123", {"start": v(-10.42, 13.87) * mm, "mid": v(-9.98, 14.93) * mm, "end": v(-8.92, 15.37) * mm});
            skArc(sketch, "E203.1.0.124", {"start": v(-8.92, 37.37) * mm, "mid": v(-9.98, 37.8) * mm, "end": v(-10.42, 38.87) * mm});
            skLineSegment(sketch, "E203.1.0.125", {"start": v(-7.42, 14.37) * mm, "end": v(-7.42, 17.87) * mm});
            skLineSegment(sketch, "E203.1.0.126", {"start": v(6.58, -36.63) * mm, "end": v(6.58, -33.13) * mm});
            skLineSegment(sketch, "E203.1.0.127", {"start": v(-8.92, -1.63) * mm, "end": v(-7.42, -1.63) * mm});
            skLineSegment(sketch, "E203.1.0.128", {"start": v(-7.42, 34.87) * mm, "end": v(-7.42, 38.37) * mm});
            skLineSegment(sketch, "E203.1.0.129", {"start": v(8.58, 14.37) * mm, "end": v(8.58, 17.87) * mm});
            skLineSegment(sketch, "E203.1.0.130", {"start": v(-8.92, 3.37) * mm, "end": v(-7.42, 3.37) * mm});
            skArc(sketch, "E203.1.0.131", {"start": v(-9.42, 39.87) * mm, "mid": v(-8.98, 38.8) * mm, "end": v(-7.92, 38.37) * mm});
            skArc(sketch, "E203.1.0.132", {"start": v(10.08, -18.63) * mm, "mid": v(11.14, -19.07) * mm, "end": v(11.58, -20.13) * mm});
            skArc(sketch, "E203.1.0.133", {"start": v(-7.92, -19.63) * mm, "mid": v(-8.98, -20.07) * mm, "end": v(-9.42, -21.13) * mm});
            skLineSegment(sketch, "E203.1.0.134", {"start": v(-5.42, 14.37) * mm, "end": v(-5.42, 17.87) * mm});
            skArc(sketch, "E203.1.0.135", {"start": v(10.58, 22.87) * mm, "mid": v(10.14, 21.8) * mm, "end": v(9.08, 21.37) * mm});
            skLineSegment(sketch, "E203.1.0.136", {"start": v(-7.42, 0.87) * mm, "end": v(-7.42, -2.63) * mm});
            skLineSegment(sketch, "E203.1.0.137", {"start": v(-7.42, -33.13) * mm, "end": v(-7.42, -29.63) * mm});
            skLineSegment(sketch, "E203.1.0.138", {"start": v(-8.92, 32.37) * mm, "end": v(-7.42, 32.37) * mm});
            skLineSegment(sketch, "E203.1.0.139", {"start": v(-5.42, 34.87) * mm, "end": v(-5.42, 31.37) * mm});
            skArc(sketch, "E203.1.0.140", {"start": v(10.08, 20.37) * mm, "mid": v(11.14, 20.8) * mm, "end": v(11.58, 21.87) * mm});
            skLineSegment(sketch, "E203.1.0.141", {"start": v(-7.42, 0.87) * mm, "end": v(-7.42, 4.37) * mm});
            skArc(sketch, "E203.1.0.142", {"start": v(-8.92, -1.63) * mm, "mid": v(-9.98, -2.07) * mm, "end": v(-10.42, -3.13) * mm});
            skArc(sketch, "E203.1.0.143", {"start": v(10.08, 49.37) * mm, "mid": v(11.14, 48.93) * mm, "end": v(11.58, 47.87) * mm});
            skLineSegment(sketch, "E203.1.0.144", {"start": v(-8.92, -30.63) * mm, "end": v(-7.42, -30.63) * mm});
            skArc(sketch, "E203.1.0.145", {"start": v(-10.42, -20.13) * mm, "mid": v(-9.98, -19.07) * mm, "end": v(-8.92, -18.63) * mm});
            skArc(sketch, "E203.1.0.146", {"start": v(9.08, 31.37) * mm, "mid": v(10.14, 30.93) * mm, "end": v(10.58, 29.87) * mm});
            skLineSegment(sketch, "E203.1.0.147", {"start": v(-5.42, -12.63) * mm, "end": v(-5.42, -16.13) * mm});
            skArc(sketch, "E203.1.0.148", {"start": v(-8.92, -30.63) * mm, "mid": v(-9.98, -30.2) * mm, "end": v(-10.42, -29.13) * mm});
            skLineSegment(sketch, "E203.1.0.149", {"start": v(-7.42, 34.87) * mm, "end": v(-7.42, 31.37) * mm});
            skArc(sketch, "E203.1.0.150", {"start": v(11.58, 30.87) * mm, "mid": v(11.14, 31.93) * mm, "end": v(10.08, 32.37) * mm});
            skLineSegment(sketch, "E203.1.0.151", {"start": v(10.08, 32.37) * mm, "end": v(8.58, 32.37) * mm});
            skArc(sketch, "E203.1.0.152", {"start": v(-8.92, 32.37) * mm, "mid": v(-9.98, 31.93) * mm, "end": v(-10.42, 30.87) * mm});
            skLineSegment(sketch, "E203.1.0.153", {"start": v(-7.42, 21.37) * mm, "end": v(-7.42, 17.87) * mm});
            skLineSegment(sketch, "E203.1.0.154", {"start": v(-8.92, -18.63) * mm, "end": v(-7.42, -18.63) * mm});
            skLineSegment(sketch, "E203.1.0.155", {"start": v(-5.42, -33.13) * mm, "end": v(-5.42, -36.63) * mm});
            skLineSegment(sketch, "E203.1.0.156", {"start": v(-8.92, 37.37) * mm, "end": v(-7.42, 37.37) * mm});
            skLineSegment(sketch, "E203.1.0.157", {"start": v(6.58, 14.37) * mm, "end": v(6.58, 17.87) * mm});
            skArc(sketch, "E203.1.0.158", {"start": v(-7.92, 21.37) * mm, "mid": v(-8.98, 21.8) * mm, "end": v(-9.42, 22.87) * mm});
            skLineSegment(sketch, "E203.1.0.159", {"start": v(-8.92, 20.37) * mm, "end": v(-7.42, 20.37) * mm});
            skArc(sketch, "E203.1.0.160", {"start": v(10.58, -21.13) * mm, "mid": v(10.14, -20.07) * mm, "end": v(9.08, -19.63) * mm});
            skLineSegment(sketch, "E203.1.0.161", {"start": v(-7.42, -19.63) * mm, "end": v(-7.42, -16.13) * mm});
            skLineSegment(sketch, "E203.1.0.162", {"start": v(10.08, 20.37) * mm, "end": v(8.58, 20.37) * mm});
            skLineSegment(sketch, "E203.1.0.163", {"start": v(6.58, -19.63) * mm, "end": v(6.58, -16.13) * mm});
            skLineSegment(sketch, "E203.1.0.164", {"start": v(8.58, 31.37) * mm, "end": v(8.58, 34.87) * mm});
            skArc(sketch, "E203.1.0.165", {"start": v(-9.42, 29.87) * mm, "mid": v(-8.98, 30.93) * mm, "end": v(-7.92, 31.37) * mm});
            skArc(sketch, "E203.1.0.166", {"start": v(10.58, 12.87) * mm, "mid": v(10.14, 13.93) * mm, "end": v(9.08, 14.37) * mm});
            skLineSegment(sketch, "E203.1.0.167", {"start": v(8.58, -19.63) * mm, "end": v(8.58, -16.13) * mm});
            skArc(sketch, "E203.1.0.168", {"start": v(-10.42, 21.87) * mm, "mid": v(-9.98, 20.8) * mm, "end": v(-8.92, 20.37) * mm});
            skLineSegment(sketch, "E203.1.0.169", {"start": v(-8.92, 15.37) * mm, "end": v(-7.42, 15.37) * mm});
            skArc(sketch, "E203.1.0.170", {"start": v(-9.42, -4.13) * mm, "mid": v(-8.98, -3.07) * mm, "end": v(-7.92, -2.63) * mm});
            skArc(sketch, "E203.1.0.171", {"start": v(-7.92, 14.37) * mm, "mid": v(-8.98, 13.93) * mm, "end": v(-9.42, 12.87) * mm});
            skLineSegment(sketch, "E203.1.0.172", {"start": v(10.08, 15.37) * mm, "end": v(8.58, 15.37) * mm});
            skLineSegment(sketch, "E203.1.0.173", {"start": v(6.58, 31.37) * mm, "end": v(6.58, 34.87) * mm});
            skLineSegment(sketch, "E203.1.0.174", {"start": v(6.58, 38.37) * mm, "end": v(6.58, 34.87) * mm});
            skLineSegment(sketch, "E203.1.0.175", {"start": v(-5.42, -33.13) * mm, "end": v(-5.42, -29.63) * mm});
            skArc(sketch, "E203.1.0.176", {"start": v(9.08, -2.63) * mm, "mid": v(10.14, -3.07) * mm, "end": v(10.58, -4.13) * mm});
            skArc(sketch, "E203.1.0.177", {"start": v(-7.92, -12.63) * mm, "mid": v(-8.98, -12.2) * mm, "end": v(-9.42, -11.13) * mm});
            skLineSegment(sketch, "E203.1.0.178", {"start": v(8.58, -36.63) * mm, "end": v(8.58, -33.13) * mm});
            skLineSegment(sketch, "E203.1.0.179", {"start": v(8.58, 4.37) * mm, "end": v(8.58, 0.87) * mm});
            skArc(sketch, "E203.1.0.180", {"start": v(10.08, -13.63) * mm, "mid": v(11.14, -13.2) * mm, "end": v(11.58, -12.13) * mm});
            skLineSegment(sketch, "E203.1.0.181", {"start": v(8.58, -29.63) * mm, "end": v(8.58, -33.13) * mm});
            skArc(sketch, "E203.1.0.182", {"start": v(11.58, -3.13) * mm, "mid": v(11.14, -2.07) * mm, "end": v(10.08, -1.63) * mm});
            skLineSegment(sketch, "E203.1.0.183", {"start": v(6.58, -12.63) * mm, "end": v(6.58, -16.13) * mm});
            skArc(sketch, "E203.1.0.184", {"start": v(9.08, 38.37) * mm, "mid": v(10.14, 38.8) * mm, "end": v(10.58, 39.87) * mm});
            skLineSegment(sketch, "E203.1.0.185", {"start": v(8.58, -12.63) * mm, "end": v(8.58, -16.13) * mm});
            skLineSegment(sketch, "E203.1.0.186", {"start": v(10.08, 3.37) * mm, "end": v(8.58, 3.37) * mm});
            skArc(sketch, "E203.1.0.187", {"start": v(-10.42, -12.13) * mm, "mid": v(-9.98, -13.2) * mm, "end": v(-8.92, -13.63) * mm});
            skArc(sketch, "E203.1.0.188", {"start": v(11.58, 38.87) * mm, "mid": v(11.14, 37.8) * mm, "end": v(10.08, 37.37) * mm});
            skArc(sketch, "E203.1.0.189", {"start": v(11.58, -29.13) * mm, "mid": v(11.14, -30.2) * mm, "end": v(10.08, -30.63) * mm});
            skLineSegment(sketch, "E203.1.0.190", {"start": v(-7.42, -12.63) * mm, "end": v(-7.42, -16.13) * mm});
            skLineSegment(sketch, "E203.1.0.191", {"start": v(8.58, -2.63) * mm, "end": v(8.58, 0.87) * mm});
            skLineSegment(sketch, "E203.1.0.192", {"start": v(8.58, 38.37) * mm, "end": v(8.58, 34.87) * mm});
            skLineSegment(sketch, "E203.1.0.193", {"start": v(10.08, -13.63) * mm, "end": v(8.58, -13.63) * mm});
            skArc(sketch, "E203.1.0.194", {"start": v(9.08, -29.63) * mm, "mid": v(10.14, -29.2) * mm, "end": v(10.58, -28.13) * mm});
            skLineSegment(sketch, "E203.1.0.195", {"start": v(-8.92, -13.63) * mm, "end": v(-7.42, -13.63) * mm});
            skLineSegment(sketch, "E203.1.0.196", {"start": v(10.08, 37.37) * mm, "end": v(8.58, 37.37) * mm});
            skLineSegment(sketch, "E203.1.0.197", {"start": v(10.08, -18.63) * mm, "end": v(8.58, -18.63) * mm});
            skArc(sketch, "E203.1.0.198", {"start": v(10.58, -11.13) * mm, "mid": v(10.14, -12.2) * mm, "end": v(9.08, -12.63) * mm});
            skArc(sketch, "E203.1.0.199", {"start": v(9.08, -36.63) * mm, "mid": v(10.14, -37.07) * mm, "end": v(10.58, -38.13) * mm});
            skLineSegment(sketch, "E203.1.0.200", {"start": v(-7.42, -33.13) * mm, "end": v(-7.42, -36.63) * mm});
            skArc(sketch, "E203.1.0.201", {"start": v(-9.42, -38.13) * mm, "mid": v(-8.98, -37.07) * mm, "end": v(-7.92, -36.63) * mm});
            skArc(sketch, "E203.1.0.202", {"start": v(-8.92, -35.63) * mm, "mid": v(-9.98, -36.07) * mm, "end": v(-10.42, -37.13) * mm});
            skArc(sketch, "E203.1.0.203", {"start": v(9.08, 4.37) * mm, "mid": v(10.14, 4.8) * mm, "end": v(10.58, 5.87) * mm});
            skArc(sketch, "E203.1.0.204", {"start": v(11.58, -37.13) * mm, "mid": v(11.14, -36.07) * mm, "end": v(10.08, -35.63) * mm});
            skArc(sketch, "E203.1.0.205", {"start": v(11.58, 4.87) * mm, "mid": v(11.14, 3.8) * mm, "end": v(10.08, 3.37) * mm});
            skLineSegment(sketch, "E203.1.0.206", {"start": v(-8.92, -35.63) * mm, "end": v(-7.42, -35.63) * mm});
            skLineSegment(sketch, "E203.1.0.207", {"start": v(10.08, -1.63) * mm, "end": v(8.58, -1.63) * mm});
            skLineSegment(sketch, "E203.1.0.208", {"start": v(10.08, -30.63) * mm, "end": v(8.58, -30.63) * mm});
            skLineSegment(sketch, "E203.1.0.209", {"start": v(10.08, -35.63) * mm, "end": v(8.58, -35.63) * mm});
            skPoint(sketch, "E203.2.0.0", {"position": v(34.58, -18.63) * mm});
            skPoint(sketch, "E203.2.0.1", {"position": v(24.58, 26.37) * mm});
            skPoint(sketch, "E203.2.0.2", {"position": v(14.58, -47.63) * mm});
            skPoint(sketch, "E203.2.0.3", {"position": v(14.58, 39.37) * mm});
            skLineSegment(sketch, "E203.2.0.4", {"start": v(19.58, 48.37) * mm, "end": v(19.58, 38.37) * mm});
            skLineSegment(sketch, "E203.2.0.5", {"start": v(18.58, -13.63) * mm, "end": v(30.58, -13.63) * mm});
            skPoint(sketch, "E203.2.0.6", {"position": v(13.58, 3.37) * mm});
            skPoint(sketch, "E203.2.0.7", {"position": v(34.58, -37.63) * mm});
            skPoint(sketch, "E203.2.0.8", {"position": v(14.58, 30.37) * mm});
            skPoint(sketch, "E203.2.0.9", {"position": v(24.58, 43.37) * mm});
            skLineSegment(sketch, "E203.2.0.10", {"start": v(33.08, -2.63) * mm, "end": v(16.08, -2.63) * mm});
            skLineSegment(sketch, "E203.2.0.11", {"start": v(19.58, -19.63) * mm, "end": v(19.58, -29.63) * mm});
            skLineSegment(sketch, "E203.2.0.12", {"start": v(33.08, 31.37) * mm, "end": v(16.08, 31.37) * mm});
            skLineSegment(sketch, "E203.2.0.13", {"start": v(18.58, 20.37) * mm, "end": v(30.58, 20.37) * mm});
            skPoint(sketch, "E203.2.0.14", {"position": v(14.58, 5.37) * mm});
            skPoint(sketch, "E203.2.0.15", {"position": v(13.58, -1.63) * mm});
            skPoint(sketch, "E203.2.0.16", {"position": v(14.58, -37.63) * mm});
            skPoint(sketch, "E203.2.0.17", {"position": v(13.58, 32.37) * mm});
            skPoint(sketch, "E203.2.0.18", {"position": v(13.58, 37.37) * mm});
            skLineSegment(sketch, "E203.2.0.19", {"start": v(33.08, -12.63) * mm, "end": v(16.08, -12.63) * mm});
            skLineSegment(sketch, "E203.2.0.20", {"start": v(29.58, 4.37) * mm, "end": v(29.58, 14.37) * mm});
            skLineSegment(sketch, "E203.2.0.21", {"start": v(18.58, 15.37) * mm, "end": v(30.58, 15.37) * mm});
            skPoint(sketch, "E203.2.0.22", {"position": v(34.58, -28.63) * mm});
            skPoint(sketch, "E203.2.0.23", {"position": v(34.58, -47.63) * mm});
            skPoint(sketch, "E203.2.0.24", {"position": v(13.58, 15.37) * mm});
            skPoint(sketch, "E203.2.0.25", {"position": v(13.58, 20.37) * mm});
            skPoint(sketch, "E203.2.0.26", {"position": v(13.58, -13.63) * mm});
            skLineSegment(sketch, "E203.2.0.27", {"start": v(29.58, -36.63) * mm, "end": v(29.58, -46.63) * mm});
            skPoint(sketch, "E203.2.0.28", {"position": v(18.58, -14.38) * mm});
            skLineSegment(sketch, "E203.2.0.29", {"start": v(33.08, 21.37) * mm, "end": v(16.08, 21.37) * mm});
            skLineSegment(sketch, "E203.2.0.30", {"start": v(18.58, -18.63) * mm, "end": v(30.58, -18.63) * mm});
            skLineSegment(sketch, "E203.2.0.31", {"start": v(18.58, 37.37) * mm, "end": v(30.58, 37.37) * mm});
            skPoint(sketch, "E203.2.0.32", {"position": v(14.58, -18.63) * mm});
            skPoint(sketch, "E203.2.0.33", {"position": v(24.58, -41.63) * mm});
            skPoint(sketch, "E203.2.0.34", {"position": v(34.58, 30.37) * mm});
            skPoint(sketch, "E203.2.0.35", {"position": v(24.58, 9.37) * mm});
            skPoint(sketch, "E203.2.0.36", {"position": v(30.58, 16.12) * mm});
            skLineSegment(sketch, "E203.2.0.37", {"start": v(19.58, 21.37) * mm, "end": v(19.58, 31.37) * mm});
            skLineSegment(sketch, "E203.2.0.38", {"start": v(29.58, -2.63) * mm, "end": v(29.58, -12.63) * mm});
            skPoint(sketch, "E203.2.0.39", {"position": v(34.58, 20.37) * mm});
            skPoint(sketch, "E203.2.0.40", {"position": v(34.58, 5.37) * mm});
            skLineSegment(sketch, "E203.2.0.41", {"start": v(33.08, -29.63) * mm, "end": v(16.08, -29.63) * mm});
            skPoint(sketch, "E203.2.0.42", {"position": v(30.58, -17.88) * mm});
            skPoint(sketch, "E203.2.0.43", {"position": v(13.58, -47.63) * mm});
            skPoint(sketch, "E203.2.0.44", {"position": v(14.58, 15.37) * mm});
            skPoint(sketch, "E203.2.0.45", {"position": v(14.58, 20.37) * mm});
            skLineSegment(sketch, "E203.2.0.46", {"start": v(18.58, -30.63) * mm, "end": v(30.58, -30.63) * mm});
            skLineSegment(sketch, "E203.2.0.47", {"start": v(29.58, 31.37) * mm, "end": v(29.58, 21.37) * mm});
            skLineSegment(sketch, "E203.2.0.48", {"start": v(33.08, 38.37) * mm, "end": v(16.08, 38.37) * mm});
            skPoint(sketch, "E203.2.0.49", {"position": v(14.58, -3.63) * mm});
            skPoint(sketch, "E203.2.0.50", {"position": v(34.58, 15.37) * mm});
            skLineSegment(sketch, "E203.2.0.51", {"start": v(33.08, 14.37) * mm, "end": v(16.08, 14.37) * mm});
            skPoint(sketch, "E203.2.0.52", {"position": v(14.58, -28.63) * mm});
            skLineSegment(sketch, "E203.2.0.53", {"start": v(18.58, 3.37) * mm, "end": v(30.58, 3.37) * mm});
            skLineSegment(sketch, "E203.2.0.54", {"start": v(19.58, -12.63) * mm, "end": v(19.58, -2.63) * mm});
            skLineSegment(sketch, "E203.2.0.55", {"start": v(29.58, -29.63) * mm, "end": v(29.58, -19.63) * mm});
            skLineSegment(sketch, "E203.2.0.56", {"start": v(29.58, 38.37) * mm, "end": v(29.58, 48.37) * mm});
            skPoint(sketch, "E203.2.0.57", {"position": v(13.58, -35.63) * mm});
            skPoint(sketch, "E203.2.0.58", {"position": v(24.58, -7.63) * mm});
            skPoint(sketch, "E203.2.0.59", {"position": v(34.58, -3.63) * mm});
            skLineSegment(sketch, "E203.2.0.60", {"start": v(33.08, -19.63) * mm, "end": v(16.08, -19.63) * mm});
            skLineSegment(sketch, "E203.2.0.61", {"start": v(19.58, 14.37) * mm, "end": v(19.58, 4.37) * mm});
            skPoint(sketch, "E203.2.0.62", {"position": v(34.58, -13.63) * mm});
            skPoint(sketch, "E203.2.0.63", {"position": v(13.58, -30.63) * mm});
            skLineSegment(sketch, "E203.2.0.64", {"start": v(18.58, -1.63) * mm, "end": v(30.58, -1.63) * mm});
            skPoint(sketch, "E203.2.0.65", {"position": v(24.58, -24.63) * mm});
            skLineSegment(sketch, "E203.2.0.66", {"start": v(33.08, 4.37) * mm, "end": v(16.08, 4.37) * mm});
            skPoint(sketch, "E203.2.0.67", {"position": v(13.58, -18.63) * mm});
            skLineSegment(sketch, "E203.2.0.68", {"start": v(34.08, 49.37) * mm, "end": v(15.08, 49.37) * mm});
            skLineSegment(sketch, "E203.2.0.69", {"start": v(18.58, 32.37) * mm, "end": v(30.58, 32.37) * mm});
            skPoint(sketch, "E203.2.0.70", {"position": v(34.58, 39.37) * mm});
            skPoint(sketch, "E203.2.0.71", {"position": v(14.58, -13.63) * mm});
            skLineSegment(sketch, "E203.2.0.72", {"start": v(13.58, -12.13) * mm, "end": v(13.58, -3.13) * mm});
            skLineSegment(sketch, "E203.2.0.73", {"start": v(34.58, -4.13) * mm, "end": v(34.58, -11.13) * mm});
            skLineSegment(sketch, "E203.2.0.74", {"start": v(33.08, 48.37) * mm, "end": v(16.08, 48.37) * mm});
            skLineSegment(sketch, "E203.2.0.75", {"start": v(35.58, -12.13) * mm, "end": v(35.58, -3.13) * mm});
            skLineSegment(sketch, "E203.2.0.76", {"start": v(33.08, -36.63) * mm, "end": v(16.08, -36.63) * mm});
            skLineSegment(sketch, "E203.2.0.77", {"start": v(33.08, -46.63) * mm, "end": v(16.08, -46.63) * mm});
            skLineSegment(sketch, "E203.2.0.78", {"start": v(19.58, -46.63) * mm, "end": v(19.58, -36.63) * mm});
            skLineSegment(sketch, "E203.2.0.79", {"start": v(34.08, -47.63) * mm, "end": v(15.08, -47.63) * mm});
            skLineSegment(sketch, "E203.2.0.80", {"start": v(14.58, -4.13) * mm, "end": v(14.58, -11.13) * mm});
            skLineSegment(sketch, "E203.2.0.81", {"start": v(18.58, -35.63) * mm, "end": v(30.58, -35.63) * mm});
            skLineSegment(sketch, "E203.2.0.82", {"start": v(13.58, -20.13) * mm, "end": v(13.58, -29.13) * mm});
            skLineSegment(sketch, "E203.2.0.83", {"start": v(34.58, -28.13) * mm, "end": v(34.58, -21.13) * mm});
            skLineSegment(sketch, "E203.2.0.84", {"start": v(13.58, 21.87) * mm, "end": v(13.58, 30.87) * mm});
            skLineSegment(sketch, "E203.2.0.85", {"start": v(35.58, 21.87) * mm, "end": v(35.58, 30.87) * mm});
            skLineSegment(sketch, "E203.2.0.86", {"start": v(14.58, -28.13) * mm, "end": v(14.58, -21.13) * mm});
            skLineSegment(sketch, "E203.2.0.87", {"start": v(13.58, -46.13) * mm, "end": v(13.58, -37.13) * mm});
            skLineSegment(sketch, "E203.2.0.88", {"start": v(14.58, -38.13) * mm, "end": v(14.58, -45.13) * mm});
            skLineSegment(sketch, "E203.2.0.89", {"start": v(14.58, 29.87) * mm, "end": v(14.58, 22.87) * mm});
            skLineSegment(sketch, "E203.2.0.90", {"start": v(35.58, -20.13) * mm, "end": v(35.58, -29.13) * mm});
            skLineSegment(sketch, "E203.2.0.91", {"start": v(34.58, 29.87) * mm, "end": v(34.58, 22.87) * mm});
            skLineSegment(sketch, "E203.2.0.92", {"start": v(13.58, 13.87) * mm, "end": v(13.58, 4.87) * mm});
            skLineSegment(sketch, "E203.2.0.93", {"start": v(30.58, -2.63) * mm, "end": v(30.58, 0.87) * mm});
            skLineSegment(sketch, "E203.2.0.94", {"start": v(14.58, 39.87) * mm, "end": v(14.58, 46.87) * mm});
            skArc(sketch, "E203.2.0.95", {"start": v(13.58, 47.87) * mm, "mid": v(14.02, 48.93) * mm, "end": v(15.08, 49.37) * mm});
            skLineSegment(sketch, "E203.2.0.96", {"start": v(30.58, 21.37) * mm, "end": v(30.58, 17.87) * mm});
            skLineSegment(sketch, "E203.2.0.97", {"start": v(30.58, 4.37) * mm, "end": v(30.58, 0.87) * mm});
            skLineSegment(sketch, "E203.2.0.98", {"start": v(13.58, 47.87) * mm, "end": v(13.58, 38.87) * mm});
            skLineSegment(sketch, "E203.2.0.99", {"start": v(30.58, -29.63) * mm, "end": v(30.58, -33.13) * mm});
            skLineSegment(sketch, "E203.2.0.100", {"start": v(18.58, 21.37) * mm, "end": v(18.58, 17.87) * mm});
            skLineSegment(sketch, "E203.2.0.101", {"start": v(18.58, 34.87) * mm, "end": v(18.58, 38.37) * mm});
            skLineSegment(sketch, "E203.2.0.102", {"start": v(18.58, 0.87) * mm, "end": v(18.58, 4.37) * mm});
            skArc(sketch, "E203.2.0.103", {"start": v(16.08, 48.37) * mm, "mid": v(15.02, 47.93) * mm, "end": v(14.58, 46.87) * mm});
            skArc(sketch, "E203.2.0.104", {"start": v(15.08, 3.37) * mm, "mid": v(14.02, 3.8) * mm, "end": v(13.58, 4.87) * mm});
            skLineSegment(sketch, "E203.2.0.105", {"start": v(35.58, 13.87) * mm, "end": v(35.58, 4.87) * mm});
            skArc(sketch, "E203.2.0.106", {"start": v(14.58, 5.87) * mm, "mid": v(15.02, 4.8) * mm, "end": v(16.08, 4.37) * mm});
            skLineSegment(sketch, "E203.2.0.107", {"start": v(34.58, 39.87) * mm, "end": v(34.58, 46.87) * mm});
            skLineSegment(sketch, "E203.2.0.108", {"start": v(18.58, -19.63) * mm, "end": v(18.58, -16.13) * mm});
            skArc(sketch, "E203.2.0.109", {"start": v(34.08, -47.63) * mm, "mid": v(35.14, -47.2) * mm, "end": v(35.58, -46.13) * mm});
            skArc(sketch, "E203.2.0.110", {"start": v(13.58, -46.13) * mm, "mid": v(14.02, -47.2) * mm, "end": v(15.08, -47.63) * mm});
            skArc(sketch, "E203.2.0.111", {"start": v(34.58, -45.13) * mm, "mid": v(34.14, -46.2) * mm, "end": v(33.08, -46.63) * mm});
            skArc(sketch, "E203.2.0.112", {"start": v(16.08, -46.63) * mm, "mid": v(15.02, -46.2) * mm, "end": v(14.58, -45.13) * mm});
            skLineSegment(sketch, "E203.2.0.113", {"start": v(34.58, -38.13) * mm, "end": v(34.58, -45.13) * mm});
            skLineSegment(sketch, "E203.2.0.114", {"start": v(35.58, -46.13) * mm, "end": v(35.58, -37.13) * mm});
            skLineSegment(sketch, "E203.2.0.115", {"start": v(35.58, 47.87) * mm, "end": v(35.58, 38.87) * mm});
            skLineSegment(sketch, "E203.2.0.116", {"start": v(18.58, 0.87) * mm, "end": v(18.58, -2.63) * mm});
            skLineSegment(sketch, "E203.2.0.117", {"start": v(14.58, 5.87) * mm, "end": v(14.58, 12.87) * mm});
            skLineSegment(sketch, "E203.2.0.118", {"start": v(34.58, 5.87) * mm, "end": v(34.58, 12.87) * mm});
            skArc(sketch, "E203.2.0.119", {"start": v(34.08, 15.37) * mm, "mid": v(35.14, 14.93) * mm, "end": v(35.58, 13.87) * mm});
            skArc(sketch, "E203.2.0.120", {"start": v(14.58, -28.13) * mm, "mid": v(15.02, -29.2) * mm, "end": v(16.08, -29.63) * mm});
            skArc(sketch, "E203.2.0.121", {"start": v(34.58, 46.87) * mm, "mid": v(34.14, 47.93) * mm, "end": v(33.08, 48.37) * mm});
            skLineSegment(sketch, "E203.2.0.122", {"start": v(32.58, 21.37) * mm, "end": v(32.58, 17.87) * mm});
            skArc(sketch, "E203.2.0.123", {"start": v(13.58, 13.87) * mm, "mid": v(14.02, 14.93) * mm, "end": v(15.08, 15.37) * mm});
            skArc(sketch, "E203.2.0.124", {"start": v(15.08, 37.37) * mm, "mid": v(14.02, 37.8) * mm, "end": v(13.58, 38.87) * mm});
            skLineSegment(sketch, "E203.2.0.125", {"start": v(16.58, 14.37) * mm, "end": v(16.58, 17.87) * mm});
            skLineSegment(sketch, "E203.2.0.126", {"start": v(30.58, -36.63) * mm, "end": v(30.58, -33.13) * mm});
            skLineSegment(sketch, "E203.2.0.127", {"start": v(15.08, -1.63) * mm, "end": v(16.58, -1.63) * mm});
            skLineSegment(sketch, "E203.2.0.128", {"start": v(16.58, 34.87) * mm, "end": v(16.58, 38.37) * mm});
            skLineSegment(sketch, "E203.2.0.129", {"start": v(32.58, 14.37) * mm, "end": v(32.58, 17.87) * mm});
            skLineSegment(sketch, "E203.2.0.130", {"start": v(15.08, 3.37) * mm, "end": v(16.58, 3.37) * mm});
            skArc(sketch, "E203.2.0.131", {"start": v(14.58, 39.87) * mm, "mid": v(15.02, 38.8) * mm, "end": v(16.08, 38.37) * mm});
            skArc(sketch, "E203.2.0.132", {"start": v(34.08, -18.63) * mm, "mid": v(35.14, -19.07) * mm, "end": v(35.58, -20.13) * mm});
            skArc(sketch, "E203.2.0.133", {"start": v(16.08, -19.63) * mm, "mid": v(15.02, -20.07) * mm, "end": v(14.58, -21.13) * mm});
            skLineSegment(sketch, "E203.2.0.134", {"start": v(18.58, 14.37) * mm, "end": v(18.58, 17.87) * mm});
            skArc(sketch, "E203.2.0.135", {"start": v(34.58, 22.87) * mm, "mid": v(34.14, 21.8) * mm, "end": v(33.08, 21.37) * mm});
            skLineSegment(sketch, "E203.2.0.136", {"start": v(16.58, 0.87) * mm, "end": v(16.58, -2.63) * mm});
            skLineSegment(sketch, "E203.2.0.137", {"start": v(16.58, -33.13) * mm, "end": v(16.58, -29.63) * mm});
            skLineSegment(sketch, "E203.2.0.138", {"start": v(15.08, 32.37) * mm, "end": v(16.58, 32.37) * mm});
            skLineSegment(sketch, "E203.2.0.139", {"start": v(18.58, 34.87) * mm, "end": v(18.58, 31.37) * mm});
            skArc(sketch, "E203.2.0.140", {"start": v(34.08, 20.37) * mm, "mid": v(35.14, 20.8) * mm, "end": v(35.58, 21.87) * mm});
            skLineSegment(sketch, "E203.2.0.141", {"start": v(16.58, 0.87) * mm, "end": v(16.58, 4.37) * mm});
            skArc(sketch, "E203.2.0.142", {"start": v(15.08, -1.63) * mm, "mid": v(14.02, -2.07) * mm, "end": v(13.58, -3.13) * mm});
            skArc(sketch, "E203.2.0.143", {"start": v(34.08, 49.37) * mm, "mid": v(35.14, 48.93) * mm, "end": v(35.58, 47.87) * mm});
            skLineSegment(sketch, "E203.2.0.144", {"start": v(15.08, -30.63) * mm, "end": v(16.58, -30.63) * mm});
            skArc(sketch, "E203.2.0.145", {"start": v(13.58, -20.13) * mm, "mid": v(14.02, -19.07) * mm, "end": v(15.08, -18.63) * mm});
            skArc(sketch, "E203.2.0.146", {"start": v(33.08, 31.37) * mm, "mid": v(34.14, 30.93) * mm, "end": v(34.58, 29.87) * mm});
            skLineSegment(sketch, "E203.2.0.147", {"start": v(18.58, -12.63) * mm, "end": v(18.58, -16.13) * mm});
            skArc(sketch, "E203.2.0.148", {"start": v(15.08, -30.63) * mm, "mid": v(14.02, -30.2) * mm, "end": v(13.58, -29.13) * mm});
            skLineSegment(sketch, "E203.2.0.149", {"start": v(16.58, 34.87) * mm, "end": v(16.58, 31.37) * mm});
            skArc(sketch, "E203.2.0.150", {"start": v(35.58, 30.87) * mm, "mid": v(35.14, 31.93) * mm, "end": v(34.08, 32.37) * mm});
            skLineSegment(sketch, "E203.2.0.151", {"start": v(34.08, 32.37) * mm, "end": v(32.58, 32.37) * mm});
            skArc(sketch, "E203.2.0.152", {"start": v(15.08, 32.37) * mm, "mid": v(14.02, 31.93) * mm, "end": v(13.58, 30.87) * mm});
            skLineSegment(sketch, "E203.2.0.153", {"start": v(16.58, 21.37) * mm, "end": v(16.58, 17.87) * mm});
            skLineSegment(sketch, "E203.2.0.154", {"start": v(15.08, -18.63) * mm, "end": v(16.58, -18.63) * mm});
            skLineSegment(sketch, "E203.2.0.155", {"start": v(18.58, -33.13) * mm, "end": v(18.58, -36.63) * mm});
            skLineSegment(sketch, "E203.2.0.156", {"start": v(15.08, 37.37) * mm, "end": v(16.58, 37.37) * mm});
            skLineSegment(sketch, "E203.2.0.157", {"start": v(30.58, 14.37) * mm, "end": v(30.58, 17.87) * mm});
            skArc(sketch, "E203.2.0.158", {"start": v(16.08, 21.37) * mm, "mid": v(15.02, 21.8) * mm, "end": v(14.58, 22.87) * mm});
            skLineSegment(sketch, "E203.2.0.159", {"start": v(15.08, 20.37) * mm, "end": v(16.58, 20.37) * mm});
            skArc(sketch, "E203.2.0.160", {"start": v(34.58, -21.13) * mm, "mid": v(34.14, -20.07) * mm, "end": v(33.08, -19.63) * mm});
            skLineSegment(sketch, "E203.2.0.161", {"start": v(16.58, -19.63) * mm, "end": v(16.58, -16.13) * mm});
            skLineSegment(sketch, "E203.2.0.162", {"start": v(34.08, 20.37) * mm, "end": v(32.58, 20.37) * mm});
            skLineSegment(sketch, "E203.2.0.163", {"start": v(30.58, -19.63) * mm, "end": v(30.58, -16.13) * mm});
            skLineSegment(sketch, "E203.2.0.164", {"start": v(32.58, 31.37) * mm, "end": v(32.58, 34.87) * mm});
            skArc(sketch, "E203.2.0.165", {"start": v(14.58, 29.87) * mm, "mid": v(15.02, 30.93) * mm, "end": v(16.08, 31.37) * mm});
            skArc(sketch, "E203.2.0.166", {"start": v(34.58, 12.87) * mm, "mid": v(34.14, 13.93) * mm, "end": v(33.08, 14.37) * mm});
            skLineSegment(sketch, "E203.2.0.167", {"start": v(32.58, -19.63) * mm, "end": v(32.58, -16.13) * mm});
            skArc(sketch, "E203.2.0.168", {"start": v(13.58, 21.87) * mm, "mid": v(14.02, 20.8) * mm, "end": v(15.08, 20.37) * mm});
            skLineSegment(sketch, "E203.2.0.169", {"start": v(15.08, 15.37) * mm, "end": v(16.58, 15.37) * mm});
            skArc(sketch, "E203.2.0.170", {"start": v(14.58, -4.13) * mm, "mid": v(15.02, -3.07) * mm, "end": v(16.08, -2.63) * mm});
            skArc(sketch, "E203.2.0.171", {"start": v(16.08, 14.37) * mm, "mid": v(15.02, 13.93) * mm, "end": v(14.58, 12.87) * mm});
            skLineSegment(sketch, "E203.2.0.172", {"start": v(34.08, 15.37) * mm, "end": v(32.58, 15.37) * mm});
            skLineSegment(sketch, "E203.2.0.173", {"start": v(30.58, 31.37) * mm, "end": v(30.58, 34.87) * mm});
            skLineSegment(sketch, "E203.2.0.174", {"start": v(30.58, 38.37) * mm, "end": v(30.58, 34.87) * mm});
            skLineSegment(sketch, "E203.2.0.175", {"start": v(18.58, -33.13) * mm, "end": v(18.58, -29.63) * mm});
            skArc(sketch, "E203.2.0.176", {"start": v(33.08, -2.63) * mm, "mid": v(34.14, -3.07) * mm, "end": v(34.58, -4.13) * mm});
            skArc(sketch, "E203.2.0.177", {"start": v(16.08, -12.63) * mm, "mid": v(15.02, -12.2) * mm, "end": v(14.58, -11.13) * mm});
            skLineSegment(sketch, "E203.2.0.178", {"start": v(32.58, -36.63) * mm, "end": v(32.58, -33.13) * mm});
            skLineSegment(sketch, "E203.2.0.179", {"start": v(32.58, 4.37) * mm, "end": v(32.58, 0.87) * mm});
            skArc(sketch, "E203.2.0.180", {"start": v(34.08, -13.63) * mm, "mid": v(35.14, -13.2) * mm, "end": v(35.58, -12.13) * mm});
            skLineSegment(sketch, "E203.2.0.181", {"start": v(32.58, -29.63) * mm, "end": v(32.58, -33.13) * mm});
            skArc(sketch, "E203.2.0.182", {"start": v(35.58, -3.13) * mm, "mid": v(35.14, -2.07) * mm, "end": v(34.08, -1.63) * mm});
            skLineSegment(sketch, "E203.2.0.183", {"start": v(30.58, -12.63) * mm, "end": v(30.58, -16.13) * mm});
            skArc(sketch, "E203.2.0.184", {"start": v(33.08, 38.37) * mm, "mid": v(34.14, 38.8) * mm, "end": v(34.58, 39.87) * mm});
            skLineSegment(sketch, "E203.2.0.185", {"start": v(32.58, -12.63) * mm, "end": v(32.58, -16.13) * mm});
            skLineSegment(sketch, "E203.2.0.186", {"start": v(34.08, 3.37) * mm, "end": v(32.58, 3.37) * mm});
            skArc(sketch, "E203.2.0.187", {"start": v(13.58, -12.13) * mm, "mid": v(14.02, -13.2) * mm, "end": v(15.08, -13.63) * mm});
            skArc(sketch, "E203.2.0.188", {"start": v(35.58, 38.87) * mm, "mid": v(35.14, 37.8) * mm, "end": v(34.08, 37.37) * mm});
            skArc(sketch, "E203.2.0.189", {"start": v(35.58, -29.13) * mm, "mid": v(35.14, -30.2) * mm, "end": v(34.08, -30.63) * mm});
            skLineSegment(sketch, "E203.2.0.190", {"start": v(16.58, -12.63) * mm, "end": v(16.58, -16.13) * mm});
            skLineSegment(sketch, "E203.2.0.191", {"start": v(32.58, -2.63) * mm, "end": v(32.58, 0.87) * mm});
            skLineSegment(sketch, "E203.2.0.192", {"start": v(32.58, 38.37) * mm, "end": v(32.58, 34.87) * mm});
            skLineSegment(sketch, "E203.2.0.193", {"start": v(34.08, -13.63) * mm, "end": v(32.58, -13.63) * mm});
            skArc(sketch, "E203.2.0.194", {"start": v(33.08, -29.63) * mm, "mid": v(34.14, -29.2) * mm, "end": v(34.58, -28.13) * mm});
            skLineSegment(sketch, "E203.2.0.195", {"start": v(15.08, -13.63) * mm, "end": v(16.58, -13.63) * mm});
            skLineSegment(sketch, "E203.2.0.196", {"start": v(34.08, 37.37) * mm, "end": v(32.58, 37.37) * mm});
            skLineSegment(sketch, "E203.2.0.197", {"start": v(34.08, -18.63) * mm, "end": v(32.58, -18.63) * mm});
            skArc(sketch, "E203.2.0.198", {"start": v(34.58, -11.13) * mm, "mid": v(34.14, -12.2) * mm, "end": v(33.08, -12.63) * mm});
            skArc(sketch, "E203.2.0.199", {"start": v(33.08, -36.63) * mm, "mid": v(34.14, -37.07) * mm, "end": v(34.58, -38.13) * mm});
            skLineSegment(sketch, "E203.2.0.200", {"start": v(16.58, -33.13) * mm, "end": v(16.58, -36.63) * mm});
            skArc(sketch, "E203.2.0.201", {"start": v(14.58, -38.13) * mm, "mid": v(15.02, -37.07) * mm, "end": v(16.08, -36.63) * mm});
            skArc(sketch, "E203.2.0.202", {"start": v(15.08, -35.63) * mm, "mid": v(14.02, -36.07) * mm, "end": v(13.58, -37.13) * mm});
            skArc(sketch, "E203.2.0.203", {"start": v(33.08, 4.37) * mm, "mid": v(34.14, 4.8) * mm, "end": v(34.58, 5.87) * mm});
            skArc(sketch, "E203.2.0.204", {"start": v(35.58, -37.13) * mm, "mid": v(35.14, -36.07) * mm, "end": v(34.08, -35.63) * mm});
            skArc(sketch, "E203.2.0.205", {"start": v(35.58, 4.87) * mm, "mid": v(35.14, 3.8) * mm, "end": v(34.08, 3.37) * mm});
            skLineSegment(sketch, "E203.2.0.206", {"start": v(15.08, -35.63) * mm, "end": v(16.58, -35.63) * mm});
            skLineSegment(sketch, "E203.2.0.207", {"start": v(34.08, -1.63) * mm, "end": v(32.58, -1.63) * mm});
            skLineSegment(sketch, "E203.2.0.208", {"start": v(34.08, -30.63) * mm, "end": v(32.58, -30.63) * mm});
            skLineSegment(sketch, "E203.2.0.209", {"start": v(34.08, -35.63) * mm, "end": v(32.58, -35.63) * mm});
            skLineSegment(sketch, "E203.direction1", {"start": v(-34.42, -47.63) * mm, "end": v(-10.42, -47.63) * mm, "construction": true});
            skLineSegment(sketch, "E204.bottom", {"start": v(-41.42, 59.37) * mm, "end": v(42.58, 59.37) * mm});
            skLineSegment(sketch, "E204.top", {"start": v(-41.42, -57.63) * mm, "end": v(42.58, -57.63) * mm});
            skLineSegment(sketch, "E204.left", {"start": v(-44.42, 56.37) * mm, "end": v(-44.42, -54.63) * mm});
            skLineSegment(sketch, "E204.right", {"start": v(45.58, 56.37) * mm, "end": v(45.58, -54.63) * mm});
            skCircle(sketch, "E205", {"center": v(38.58, -47.63) * mm, "radius": 1.25 * mm});
            skCircle(sketch, "E206", {"center": v(38.58, 49.37) * mm, "radius": 1.25 * mm});
            skCircle(sketch, "E207", {"center": v(-37.42, 49.37) * mm, "radius": 1.25 * mm});
            skCircle(sketch, "E208", {"center": v(-37.42, -47.63) * mm, "radius": 1.25 * mm});
            skPoint(sketch, "E209.visualSharp", {"position": v(45.58, 59.37) * mm});
            skArc(sketch, "E209.filletArc", {"start": v(45.58, 56.37) * mm, "mid": v(44.7, 58.49) * mm, "end": v(42.58, 59.37) * mm});
            skPoint(sketch, "E210.visualSharp", {"position": v(45.58, -57.63) * mm});
            skArc(sketch, "E210.filletArc", {"start": v(42.58, -57.63) * mm, "mid": v(44.7, -56.76) * mm, "end": v(45.58, -54.63) * mm});
            skPoint(sketch, "E211.visualSharp", {"position": v(-44.42, 59.37) * mm});
            skArc(sketch, "E211.filletArc", {"start": v(-41.42, 59.37) * mm, "mid": v(-43.54, 58.49) * mm, "end": v(-44.42, 56.37) * mm});
            skPoint(sketch, "E212.visualSharp", {"position": v(-44.42, -57.63) * mm});
            skArc(sketch, "E212.filletArc", {"start": v(-44.42, -54.63) * mm, "mid": v(-43.54, -56.76) * mm, "end": v(-41.42, -57.63) * mm});
            skSolve(sketch);
        }
        {
            var Q0;
            Q0=makeQuery(id+"F0.imprint","IMPRINT",FACE,{"disambiguationData":[TD([[makeQuery(id+"F0.imprint","IMPRINT",EDGE,{"derivedFrom":sQuery(id+"F0.wireOp",EDGE,"E16.bottom")}),1.0]])]});
            extrude(context, id + "F1", {"entities" : qUnion([Q0]), "depth" : 10 * mm});
        }
        {
            var Q0;
            {var subQ9=sQuery(id+"F0.wireOp",EDGE,"E130.MirrorCS");Q0=makeQuery(id+"F0.imprint","IMPRINT",FACE,{"disambiguationData":[TD([[makeQuery(id+"F0.imprint","IMPRINT",EDGE,{"derivedFrom":subQ9}),-1.0]])]});}
            var Q1;
            {var subQ9=sQuery(id+"F0.wireOp",EDGE,"E163.MirrorCS");Q1=makeQuery(id+"F0.imprint","IMPRINT",FACE,{"disambiguationData":[TD([[makeQuery(id+"F0.imprint","IMPRINT",EDGE,{"derivedFrom":subQ9}),-1.0]])]});}
            var Q2;
            {var subQ7=sQuery(id+"F0.wireOp",EDGE,"E162.MirrorCS");Q2=makeQuery(id+"F0.imprint","IMPRINT",FACE,{"disambiguationData":[TD([[makeQuery(id+"F0.imprint","IMPRINT",EDGE,{"derivedFrom":subQ7}),-1.0]])]});}
            var Q3;
            {var subQ5=sQuery(id+"F0.wireOp",EDGE,"E184.MirrorCS");Q3=makeQuery(id+"F0.imprint","IMPRINT",FACE,{"disambiguationData":[TD([[makeQuery(id+"F0.imprint","IMPRINT",EDGE,{"derivedFrom":subQ5}),1.0]])]});}
            var Q4;
            {var subQ5=sQuery(id+"F0.wireOp",EDGE,"E129.MirrorCS");Q4=makeQuery(id+"F0.imprint","IMPRINT",FACE,{"disambiguationData":[TD([[makeQuery(id+"F0.imprint","IMPRINT",EDGE,{"derivedFrom":subQ5}),1.0]])]});}
            var Q5;
            {var subQ7=sQuery(id+"F0.wireOp",EDGE,"E200");Q5=makeQuery(id+"F0.imprint","IMPRINT",FACE,{"disambiguationData":[TD([[makeQuery(id+"F0.imprint","IMPRINT",EDGE,{"derivedFrom":subQ7}),1.0]])]});}
            var Q6;
            Q6=makeQuery(id+"F0.imprint","IMPRINT",FACE,{"disambiguationData":[TD([[makeQuery(id+"F0.imprint","IMPRINT",EDGE,{"derivedFrom":sQuery(id+"F0.wireOp",EDGE,"E203.1.0.84")}),-1.0]])]});
            var Q7;
            {var subQ3=sQuery(id+"F0.wireOp",EDGE,"E203.1.0.13");Q7=makeQuery(id+"F0.imprint","IMPRINT",FACE,{"disambiguationData":[TD([[makeQuery(id+"F0.imprint","IMPRINT",EDGE,{"derivedFrom":subQ3}),1.0]])]});}
            var Q8;
            {var subQ0=sQuery(id+"F0.wireOp",EDGE,"E203.1.0.69");Q8=makeQuery(id+"F0.imprint","IMPRINT",FACE,{"disambiguationData":[TD([[makeQuery(id+"F0.imprint","IMPRINT",EDGE,{"derivedFrom":subQ0}),-1.0]])]});}
            var Q9;
            Q9=makeQuery(id+"F0.imprint","IMPRINT",FACE,{"disambiguationData":[TD([[makeQuery(id+"F0.imprint","IMPRINT",EDGE,{"derivedFrom":sQuery(id+"F0.wireOp",EDGE,"E203.1.0.85")}),1.0]])]});
            var Q10;
            Q10=makeQuery(id+"F0.imprint","IMPRINT",FACE,{"disambiguationData":[TD([[makeQuery(id+"F0.imprint","IMPRINT",EDGE,{"derivedFrom":sQuery(id+"F0.wireOp",EDGE,"E203.1.0.68")}),1.0]])]});
            var Q11;
            {var subQ7=sQuery(id+"F0.wireOp",EDGE,"E203.1.0.31");Q11=makeQuery(id+"F0.imprint","IMPRINT",FACE,{"disambiguationData":[TD([[makeQuery(id+"F0.imprint","IMPRINT",EDGE,{"derivedFrom":subQ7}),1.0]])]});}
            var Q12;
            {var subQ7=sQuery(id+"F0.wireOp",EDGE,"E203.2.0.13");Q12=makeQuery(id+"F0.imprint","IMPRINT",FACE,{"disambiguationData":[TD([[makeQuery(id+"F0.imprint","IMPRINT",EDGE,{"derivedFrom":subQ7}),1.0]])]});}
            var Q13;
            Q13=makeQuery(id+"F0.imprint","IMPRINT",FACE,{"disambiguationData":[TD([[makeQuery(id+"F0.imprint","IMPRINT",EDGE,{"derivedFrom":sQuery(id+"F0.wireOp",EDGE,"E203.2.0.84")}),-1.0]])]});
            var Q14;
            {var subQ0=sQuery(id+"F0.wireOp",EDGE,"E203.2.0.69");Q14=makeQuery(id+"F0.imprint","IMPRINT",FACE,{"disambiguationData":[TD([[makeQuery(id+"F0.imprint","IMPRINT",EDGE,{"derivedFrom":subQ0}),-1.0]])]});}
            var Q15;
            Q15=makeQuery(id+"F0.imprint","IMPRINT",FACE,{"disambiguationData":[TD([[makeQuery(id+"F0.imprint","IMPRINT",EDGE,{"derivedFrom":sQuery(id+"F0.wireOp",EDGE,"E203.2.0.85")}),1.0]])]});
            var Q16;
            Q16=makeQuery(id+"F0.imprint","IMPRINT",FACE,{"disambiguationData":[TD([[makeQuery(id+"F0.imprint","IMPRINT",EDGE,{"derivedFrom":sQuery(id+"F0.wireOp",EDGE,"E203.2.0.68")}),1.0]])]});
            var Q17;
            {var subQ7=sQuery(id+"F0.wireOp",EDGE,"E203.2.0.31");Q17=makeQuery(id+"F0.imprint","IMPRINT",FACE,{"disambiguationData":[TD([[makeQuery(id+"F0.imprint","IMPRINT",EDGE,{"derivedFrom":subQ7}),1.0]])]});}
            var Q18;
            {var subQ3=sQuery(id+"F0.wireOp",EDGE,"E201");Q18=makeQuery(id+"F0.imprint","IMPRINT",FACE,{"disambiguationData":[TD([[makeQuery(id+"F0.imprint","IMPRINT",EDGE,{"derivedFrom":subQ3}),-1.0]])]});}
            var Q19;
            {var subQ1=sQuery(id+"F0.wireOp",EDGE,"E97.MirrorCS");Q19=makeQuery(id+"F0.imprint","IMPRINT",FACE,{"disambiguationData":[TD([[makeQuery(id+"F0.imprint","IMPRINT",EDGE,{"derivedFrom":subQ1}),-1.0]])]});}
            var Q20;
            Q20=makeQuery(id+"F0.imprint","IMPRINT",FACE,{"disambiguationData":[TD([[makeQuery(id+"F0.imprint","IMPRINT",EDGE,{"derivedFrom":sQuery(id+"F0.wireOp",EDGE,"E95.MirrorCS")}),-1.0]])]});
            var Q21;
            Q21=makeQuery(id+"F0.imprint","IMPRINT",FACE,{"disambiguationData":[TD([[makeQuery(id+"F0.imprint","IMPRINT",EDGE,{"derivedFrom":sQuery(id+"F0.wireOp",EDGE,"E203.1.0.92")}),1.0]])]});
            var Q22;
            {var subQ7=sQuery(id+"F0.wireOp",EDGE,"E203.1.0.21");Q22=makeQuery(id+"F0.imprint","IMPRINT",FACE,{"disambiguationData":[TD([[makeQuery(id+"F0.imprint","IMPRINT",EDGE,{"derivedFrom":subQ7}),-1.0]])]});}
            var Q23;
            Q23=makeQuery(id+"F0.imprint","IMPRINT",FACE,{"disambiguationData":[TD([[makeQuery(id+"F0.imprint","IMPRINT",EDGE,{"derivedFrom":sQuery(id+"F0.wireOp",EDGE,"E203.1.0.105")}),-1.0]])]});
            var Q24;
            {var subQ5=sQuery(id+"F0.wireOp",EDGE,"E203.1.0.53");Q24=makeQuery(id+"F0.imprint","IMPRINT",FACE,{"disambiguationData":[TD([[makeQuery(id+"F0.imprint","IMPRINT",EDGE,{"derivedFrom":subQ5}),1.0]])]});}
            var Q25;
            {var subQ5=sQuery(id+"F0.wireOp",EDGE,"E76.MirrorCS");Q25=makeQuery(id+"F0.imprint","IMPRINT",FACE,{"disambiguationData":[TD([[makeQuery(id+"F0.imprint","IMPRINT",EDGE,{"derivedFrom":subQ5}),-1.0]])]});}
            var Q26;
            Q26=makeQuery(id+"F0.imprint","IMPRINT",FACE,{"disambiguationData":[TD([[makeQuery(id+"F0.imprint","IMPRINT",EDGE,{"derivedFrom":sQuery(id+"F0.wireOp",EDGE,"E61.MirrorCS")}),-1.0]])]});
            var Q27;
            {var subQ7=sQuery(id+"F0.wireOp",EDGE,"E199");Q27=makeQuery(id+"F0.imprint","IMPRINT",FACE,{"disambiguationData":[TD([[makeQuery(id+"F0.imprint","IMPRINT",EDGE,{"derivedFrom":subQ7}),1.0]])]});}
            var Q28;
            Q28=makeQuery(id+"F0.imprint","IMPRINT",FACE,{"disambiguationData":[TD([[makeQuery(id+"F0.imprint","IMPRINT",EDGE,{"derivedFrom":sQuery(id+"F0.wireOp",EDGE,"E67.MirrorCS")}),1.0]])]});
            var Q29;
            Q29=makeQuery(id+"F0.imprint","IMPRINT",FACE,{"disambiguationData":[TD([[makeQuery(id+"F0.imprint","IMPRINT",EDGE,{"derivedFrom":sQuery(id+"F0.wireOp",EDGE,"E203.1.0.72")}),-1.0]])]});
            var Q30;
            {var subQ0=sQuery(id+"F0.wireOp",EDGE,"E203.1.0.64");Q30=makeQuery(id+"F0.imprint","IMPRINT",FACE,{"disambiguationData":[TD([[makeQuery(id+"F0.imprint","IMPRINT",EDGE,{"derivedFrom":subQ0}),-1.0]])]});}
            var Q31;
            {var subQ5=sQuery(id+"F0.wireOp",EDGE,"E203.1.0.5");Q31=makeQuery(id+"F0.imprint","IMPRINT",FACE,{"disambiguationData":[TD([[makeQuery(id+"F0.imprint","IMPRINT",EDGE,{"derivedFrom":subQ5}),1.0]])]});}
            var Q32;
            Q32=makeQuery(id+"F0.imprint","IMPRINT",FACE,{"disambiguationData":[TD([[makeQuery(id+"F0.imprint","IMPRINT",EDGE,{"derivedFrom":sQuery(id+"F0.wireOp",EDGE,"E203.1.0.73")}),1.0]])]});
            var Q33;
            Q33=makeQuery(id+"F0.imprint","IMPRINT",FACE,{"disambiguationData":[TD([[makeQuery(id+"F0.imprint","IMPRINT",EDGE,{"derivedFrom":sQuery(id+"F0.wireOp",EDGE,"E203.2.0.72")}),-1.0]])]});
            var Q34;
            {var subQ7=sQuery(id+"F0.wireOp",EDGE,"E203.2.0.5");Q34=makeQuery(id+"F0.imprint","IMPRINT",FACE,{"disambiguationData":[TD([[makeQuery(id+"F0.imprint","IMPRINT",EDGE,{"derivedFrom":subQ7}),1.0]])]});}
            var Q35;
            {var subQ0=sQuery(id+"F0.wireOp",EDGE,"E203.2.0.64");Q35=makeQuery(id+"F0.imprint","IMPRINT",FACE,{"disambiguationData":[TD([[makeQuery(id+"F0.imprint","IMPRINT",EDGE,{"derivedFrom":subQ0}),-1.0]])]});}
            var Q36;
            Q36=makeQuery(id+"F0.imprint","IMPRINT",FACE,{"disambiguationData":[TD([[makeQuery(id+"F0.imprint","IMPRINT",EDGE,{"derivedFrom":sQuery(id+"F0.wireOp",EDGE,"E203.2.0.92")}),1.0]])]});
            var Q37;
            {var subQ5=sQuery(id+"F0.wireOp",EDGE,"E203.2.0.53");Q37=makeQuery(id+"F0.imprint","IMPRINT",FACE,{"disambiguationData":[TD([[makeQuery(id+"F0.imprint","IMPRINT",EDGE,{"derivedFrom":subQ5}),1.0]])]});}
            var Q38;
            {var subQ7=sQuery(id+"F0.wireOp",EDGE,"E203.2.0.21");Q38=makeQuery(id+"F0.imprint","IMPRINT",FACE,{"disambiguationData":[TD([[makeQuery(id+"F0.imprint","IMPRINT",EDGE,{"derivedFrom":subQ7}),-1.0]])]});}
            var Q39;
            Q39=makeQuery(id+"F0.imprint","IMPRINT",FACE,{"disambiguationData":[TD([[makeQuery(id+"F0.imprint","IMPRINT",EDGE,{"derivedFrom":sQuery(id+"F0.wireOp",EDGE,"E203.2.0.105")}),-1.0]])]});
            var Q40;
            Q40=makeQuery(id+"F0.imprint","IMPRINT",FACE,{"disambiguationData":[TD([[makeQuery(id+"F0.imprint","IMPRINT",EDGE,{"derivedFrom":sQuery(id+"F0.wireOp",EDGE,"E203.2.0.73")}),1.0]])]});
            var Q41;
            {var subQ2=sQuery(id+"F0.wireOp",EDGE,"E27.MirrorCS");Q41=makeQuery(id+"F0.imprint","IMPRINT",FACE,{"disambiguationData":[TD([[makeQuery(id+"F0.imprint","IMPRINT",EDGE,{"derivedFrom":subQ2}),-1.0]])]});}
            var Q42;
            {var subQ0=sQuery(id+"F0.wireOp",EDGE,"E31.MirrorCS");Q42=makeQuery(id+"F0.imprint","IMPRINT",FACE,{"disambiguationData":[TD([[makeQuery(id+"F0.imprint","IMPRINT",EDGE,{"derivedFrom":subQ0}),1.0]])]});}
            var Q43;
            Q43=makeQuery(id+"F0.imprint","IMPRINT",FACE,{"disambiguationData":[TD([[makeQuery(id+"F0.imprint","IMPRINT",EDGE,{"derivedFrom":sQuery(id+"F0.wireOp",EDGE,"E32.MirrorCS")}),-1.0]])]});
            var Q44;
            {var subQ3=sQuery(id+"F0.wireOp",EDGE,"E202");Q44=makeQuery(id+"F0.imprint","IMPRINT",FACE,{"disambiguationData":[TD([[makeQuery(id+"F0.imprint","IMPRINT",EDGE,{"derivedFrom":subQ3}),-1.0]])]});}
            var Q45;
            Q45=makeQuery(id+"F0.imprint","IMPRINT",FACE,{"disambiguationData":[TD([[makeQuery(id+"F0.imprint","IMPRINT",EDGE,{"derivedFrom":sQuery(id+"F0.wireOp",EDGE,"E203.1.0.82")}),1.0]])]});
            var Q46;
            {var subQ6=sQuery(id+"F0.wireOp",EDGE,"E203.1.0.30");Q46=makeQuery(id+"F0.imprint","IMPRINT",FACE,{"disambiguationData":[TD([[makeQuery(id+"F0.imprint","IMPRINT",EDGE,{"derivedFrom":subQ6}),-1.0]])]});}
            var Q47;
            {var subQ0=sQuery(id+"F0.wireOp",EDGE,"E203.1.0.46");Q47=makeQuery(id+"F0.imprint","IMPRINT",FACE,{"disambiguationData":[TD([[makeQuery(id+"F0.imprint","IMPRINT",EDGE,{"derivedFrom":subQ0}),1.0]])]});}
            var Q48;
            Q48=makeQuery(id+"F0.imprint","IMPRINT",FACE,{"disambiguationData":[TD([[makeQuery(id+"F0.imprint","IMPRINT",EDGE,{"derivedFrom":sQuery(id+"F0.wireOp",EDGE,"E203.1.0.83")}),-1.0]])]});
            var Q49;
            {var subQ0=sQuery(id+"F0.wireOp",EDGE,"E203.1.0.81");Q49=makeQuery(id+"F0.imprint","IMPRINT",FACE,{"disambiguationData":[TD([[makeQuery(id+"F0.imprint","IMPRINT",EDGE,{"derivedFrom":subQ0}),-1.0]])]});}
            var Q50;
            Q50=makeQuery(id+"F0.imprint","IMPRINT",FACE,{"disambiguationData":[TD([[makeQuery(id+"F0.imprint","IMPRINT",EDGE,{"derivedFrom":sQuery(id+"F0.wireOp",EDGE,"E203.1.0.79")}),-1.0]])]});
            var Q51;
            {var subQ5=sQuery(id+"F0.wireOp",EDGE,"E1.MirrorCS");Q51=makeQuery(id+"F0.imprint","IMPRINT",FACE,{"disambiguationData":[TD([[makeQuery(id+"F0.imprint","IMPRINT",EDGE,{"derivedFrom":subQ5}),1.0]])]});}
            var Q52;
            {var subQ7=sQuery(id+"F0.wireOp",EDGE,"E22");Q52=makeQuery(id+"F0.imprint","IMPRINT",FACE,{"disambiguationData":[TD([[makeQuery(id+"F0.imprint","IMPRINT",EDGE,{"derivedFrom":subQ7}),-1.0]])]});}
            var Q53;
            Q53=makeQuery(id+"F0.imprint","IMPRINT",FACE,{"disambiguationData":[TD([[makeQuery(id+"F0.imprint","IMPRINT",EDGE,{"derivedFrom":sQuery(id+"F0.wireOp",EDGE,"E203.2.0.79")}),-1.0]])]});
            var Q54;
            {var subQ0=sQuery(id+"F0.wireOp",EDGE,"E203.2.0.81");Q54=makeQuery(id+"F0.imprint","IMPRINT",FACE,{"disambiguationData":[TD([[makeQuery(id+"F0.imprint","IMPRINT",EDGE,{"derivedFrom":subQ0}),-1.0]])]});}
            var Q55;
            Q55=makeQuery(id+"F0.imprint","IMPRINT",FACE,{"disambiguationData":[TD([[makeQuery(id+"F0.imprint","IMPRINT",EDGE,{"derivedFrom":sQuery(id+"F0.wireOp",EDGE,"E203.2.0.82")}),1.0]])]});
            var Q56;
            {var subQ4=sQuery(id+"F0.wireOp",EDGE,"E203.2.0.30");Q56=makeQuery(id+"F0.imprint","IMPRINT",FACE,{"disambiguationData":[TD([[makeQuery(id+"F0.imprint","IMPRINT",EDGE,{"derivedFrom":subQ4}),-1.0]])]});}
            var Q57;
            {var subQ0=sQuery(id+"F0.wireOp",EDGE,"E203.2.0.46");Q57=makeQuery(id+"F0.imprint","IMPRINT",FACE,{"disambiguationData":[TD([[makeQuery(id+"F0.imprint","IMPRINT",EDGE,{"derivedFrom":subQ0}),1.0]])]});}
            var Q58;
            Q58=makeQuery(id+"F0.imprint","IMPRINT",FACE,{"disambiguationData":[TD([[makeQuery(id+"F0.imprint","IMPRINT",EDGE,{"derivedFrom":sQuery(id+"F0.wireOp",EDGE,"E203.2.0.83")}),-1.0]])]});
            var Q59;
            {var subQ4=sQuery(id+"F0.wireOp",EDGE,"E112.MirrorCS");Q59=makeQuery(id+"F0.imprint","IMPRINT",FACE,{"disambiguationData":[TD([[makeQuery(id+"F0.imprint","IMPRINT",EDGE,{"derivedFrom":subQ4}),1.0]])]});}
            extrude(context, id + "F2", {"entities" : qUnion([Q0, Q1, Q2, Q3, Q4, Q5, Q6, Q7, Q8, Q9, Q10, Q11, Q12, Q13, Q14, Q15, Q16, Q17, Q18, Q19, Q20, Q21, Q22, Q23, Q24, Q25, Q26, Q27, Q28, Q29, Q30, Q31, Q32, Q33, Q34, Q35, Q36, Q37, Q38, Q39, Q40, Q41, Q42, Q43, Q44, Q45, Q46, Q47, Q48, Q49, Q50, Q51, Q52, Q53, Q54, Q55, Q56, Q57, Q58, Q59]), "operationType" : NewBodyOperationType.ADD, "depth" : 12.7 * mm});
        }
        {
            var Q0;
            {var subQ5=sQuery(id+"F0.wireOp",EDGE,"E152.MirrorCS");var subQ6=sQuery(id+"F0.wireOp",EDGE,"E141.MirrorCS");var subQ7=makeQuery(id+"F0.imprint","INTERSECT",VERTEX,{"derivedFrom":[subQ6,subQ5]});Q0=makeQuery(id+"F0.imprint","IMPRINT",FACE,{"disambiguationData":[TD([[makeQuery(id+"F0.imprint","IMPRINT",EDGE,{"disambiguationData":[TD([[subQ7,-1.0]])],"derivedFrom":subQ6}),-1.0]])]});}
            var Q1;
            {var subQ2=sQuery(id+"F0.wireOp",EDGE,"E141.MirrorCS");var subQ5=sQuery(id+"F0.wireOp",EDGE,"E139.MirrorCS");var subQ12=makeQuery(id+"F0.imprint","INTERSECT",VERTEX,{"derivedFrom":[subQ5,subQ2]});Q1=makeQuery(id+"F0.imprint","IMPRINT",FACE,{"disambiguationData":[TD([[makeQuery(id+"F0.imprint","IMPRINT",EDGE,{"disambiguationData":[TD([[subQ12,-1.0]])],"derivedFrom":subQ5}),-1.0]])]});}
            var Q2;
            {var subQ4=sQuery(id+"F0.wireOp",EDGE,"E203.1.0.139");var subQ7=sQuery(id+"F0.wireOp",EDGE,"E203.1.0.12");var subQ8=makeQuery(id+"F0.imprint","INTERSECT",VERTEX,{"derivedFrom":[subQ7,subQ4]});Q2=makeQuery(id+"F0.imprint","IMPRINT",FACE,{"disambiguationData":[TD([[makeQuery(id+"F0.imprint","IMPRINT",EDGE,{"disambiguationData":[TD([[subQ8,-1.0]])],"derivedFrom":subQ7}),-1.0]])]});}
            var Q3;
            {var subQ5=sQuery(id+"F0.wireOp",EDGE,"E203.1.0.164");var subQ7=sQuery(id+"F0.wireOp",EDGE,"E203.1.0.12");var subQ8=makeQuery(id+"F0.imprint","INTERSECT",VERTEX,{"derivedFrom":[subQ7,subQ5]});Q3=makeQuery(id+"F0.imprint","IMPRINT",FACE,{"disambiguationData":[TD([[makeQuery(id+"F0.imprint","IMPRINT",EDGE,{"disambiguationData":[TD([[subQ8,-1.0]])],"derivedFrom":subQ7}),-1.0]])]});}
            var Q4;
            {var subQ4=sQuery(id+"F0.wireOp",EDGE,"E203.2.0.139");var subQ8=sQuery(id+"F0.wireOp",EDGE,"E203.2.0.12");var subQ9=makeQuery(id+"F0.imprint","INTERSECT",VERTEX,{"derivedFrom":[subQ8,subQ4]});Q4=makeQuery(id+"F0.imprint","IMPRINT",FACE,{"disambiguationData":[TD([[makeQuery(id+"F0.imprint","IMPRINT",EDGE,{"disambiguationData":[TD([[subQ9,-1.0]])],"derivedFrom":subQ8}),-1.0]])]});}
            var Q5;
            {var subQ0=sQuery(id+"F0.wireOp",EDGE,"E203.2.0.164");var subQ11=sQuery(id+"F0.wireOp",EDGE,"E203.2.0.12");var subQ12=makeQuery(id+"F0.imprint","INTERSECT",VERTEX,{"derivedFrom":[subQ11,subQ0]});Q5=makeQuery(id+"F0.imprint","IMPRINT",FACE,{"disambiguationData":[TD([[makeQuery(id+"F0.imprint","IMPRINT",EDGE,{"disambiguationData":[TD([[subQ12,-1.0]])],"derivedFrom":subQ11}),-1.0]])]});}
            var Q6;
            {var subQ0=sQuery(id+"F0.wireOp",EDGE,"E203.2.0.96");var subQ2=sQuery(id+"F0.wireOp",EDGE,"E203.2.0.29");var subQ3=makeQuery(id+"F0.imprint","INTERSECT",VERTEX,{"derivedFrom":[subQ2,subQ0]});Q6=makeQuery(id+"F0.imprint","IMPRINT",FACE,{"disambiguationData":[TD([[makeQuery(id+"F0.imprint","IMPRINT",EDGE,{"disambiguationData":[TD([[subQ3,1.0]])],"derivedFrom":subQ2}),1.0]])]});}
            var Q7;
            {var subQ0=sQuery(id+"F0.wireOp",EDGE,"E203.2.0.100");var subQ2=sQuery(id+"F0.wireOp",EDGE,"E203.2.0.29");var subQ3=makeQuery(id+"F0.imprint","INTERSECT",VERTEX,{"derivedFrom":[subQ2,subQ0]});Q7=makeQuery(id+"F0.imprint","IMPRINT",FACE,{"disambiguationData":[TD([[makeQuery(id+"F0.imprint","IMPRINT",EDGE,{"disambiguationData":[TD([[subQ3,-1.0]])],"derivedFrom":subQ2}),1.0]])]});}
            var Q8;
            {var subQ0=sQuery(id+"F0.wireOp",EDGE,"E203.1.0.96");var subQ11=sQuery(id+"F0.wireOp",EDGE,"E203.1.0.29");var subQ12=makeQuery(id+"F0.imprint","INTERSECT",VERTEX,{"derivedFrom":[subQ11,subQ0]});Q8=makeQuery(id+"F0.imprint","IMPRINT",FACE,{"disambiguationData":[TD([[makeQuery(id+"F0.imprint","IMPRINT",EDGE,{"disambiguationData":[TD([[subQ12,1.0]])],"derivedFrom":subQ11}),1.0]])]});}
            var Q9;
            {var subQ0=sQuery(id+"F0.wireOp",EDGE,"E203.1.0.100");var subQ4=sQuery(id+"F0.wireOp",EDGE,"E203.1.0.29");var subQ5=makeQuery(id+"F0.imprint","INTERSECT",VERTEX,{"derivedFrom":[subQ4,subQ0]});Q9=makeQuery(id+"F0.imprint","IMPRINT",FACE,{"disambiguationData":[TD([[makeQuery(id+"F0.imprint","IMPRINT",EDGE,{"disambiguationData":[TD([[subQ5,-1.0]])],"derivedFrom":subQ4}),1.0]])]});}
            var Q10;
            {var subQ1=sQuery(id+"F0.wireOp",EDGE,"E124.MirrorCS");var subQ8=sQuery(id+"F0.wireOp",EDGE,"E113.MirrorCS");var subQ9=makeQuery(id+"F0.imprint","INTERSECT",VERTEX,{"derivedFrom":[subQ8,subQ1]});Q10=makeQuery(id+"F0.imprint","IMPRINT",FACE,{"disambiguationData":[TD([[makeQuery(id+"F0.imprint","IMPRINT",EDGE,{"disambiguationData":[TD([[subQ9,1.0]])],"derivedFrom":subQ8}),-1.0]])]});}
            var Q11;
            {var subQ1=sQuery(id+"F0.wireOp",EDGE,"E117.MirrorCS");var subQ4=sQuery(id+"F0.wireOp",EDGE,"E113.MirrorCS");var subQ5=makeQuery(id+"F0.imprint","INTERSECT",VERTEX,{"derivedFrom":[subQ4,subQ1]});Q11=makeQuery(id+"F0.imprint","IMPRINT",FACE,{"disambiguationData":[TD([[makeQuery(id+"F0.imprint","IMPRINT",EDGE,{"disambiguationData":[TD([[subQ5,1.0]])],"derivedFrom":subQ4}),-1.0]])]});}
            var Q12;
            {var subQ11=sQuery(id+"F0.wireOp",EDGE,"E70.MirrorCS");var subQ12=makeQuery(id+"F0.imprint","INTERSECT",VERTEX,{"derivedFrom":[sQuery(id+"F0.wireOp",EDGE,"E65.MirrorCS"),subQ11]});Q12=makeQuery(id+"F0.imprint","IMPRINT",FACE,{"disambiguationData":[TD([[makeQuery(id+"F0.imprint","IMPRINT",EDGE,{"disambiguationData":[TD([[subQ12,1.0]])],"derivedFrom":subQ11}),1.0]])]});}
            var Q13;
            {var subQ8=sQuery(id+"F0.wireOp",EDGE,"E82.MirrorCS");var subQ10=sQuery(id+"F0.wireOp",EDGE,"E64.MirrorCS");var subQ14=makeQuery(id+"F0.imprint","INTERSECT",VERTEX,{"derivedFrom":[subQ10,subQ8]});Q13=makeQuery(id+"F0.imprint","IMPRINT",FACE,{"disambiguationData":[TD([[makeQuery(id+"F0.imprint","IMPRINT",EDGE,{"disambiguationData":[TD([[subQ14,-1.0]])],"derivedFrom":subQ10}),-1.0]])]});}
            var Q14;
            {var subQ9=sQuery(id+"F0.wireOp",EDGE,"E203.1.0.116");var subQ11=sQuery(id+"F0.wireOp",EDGE,"E203.1.0.10");var subQ12=makeQuery(id+"F0.imprint","INTERSECT",VERTEX,{"derivedFrom":[subQ11,subQ9]});Q14=makeQuery(id+"F0.imprint","IMPRINT",FACE,{"disambiguationData":[TD([[makeQuery(id+"F0.imprint","IMPRINT",EDGE,{"disambiguationData":[TD([[subQ12,-1.0]])],"derivedFrom":subQ11}),-1.0]])]});}
            var Q15;
            {var subQ0=sQuery(id+"F0.wireOp",EDGE,"E203.1.0.93");var subQ2=sQuery(id+"F0.wireOp",EDGE,"E203.1.0.10");var subQ3=makeQuery(id+"F0.imprint","INTERSECT",VERTEX,{"derivedFrom":[subQ2,subQ0]});Q15=makeQuery(id+"F0.imprint","IMPRINT",FACE,{"disambiguationData":[TD([[makeQuery(id+"F0.imprint","IMPRINT",EDGE,{"disambiguationData":[TD([[subQ3,1.0]])],"derivedFrom":subQ2}),-1.0]])]});}
            var Q16;
            {var subQ4=sQuery(id+"F0.wireOp",EDGE,"E203.2.0.116");var subQ6=sQuery(id+"F0.wireOp",EDGE,"E203.2.0.10");var subQ7=makeQuery(id+"F0.imprint","INTERSECT",VERTEX,{"derivedFrom":[subQ6,subQ4]});Q16=makeQuery(id+"F0.imprint","IMPRINT",FACE,{"disambiguationData":[TD([[makeQuery(id+"F0.imprint","IMPRINT",EDGE,{"disambiguationData":[TD([[subQ7,-1.0]])],"derivedFrom":subQ6}),-1.0]])]});}
            var Q17;
            {var subQ8=sQuery(id+"F0.wireOp",EDGE,"E203.2.0.93");var subQ12=sQuery(id+"F0.wireOp",EDGE,"E203.2.0.10");var subQ13=makeQuery(id+"F0.imprint","INTERSECT",VERTEX,{"derivedFrom":[subQ12,subQ8]});Q17=makeQuery(id+"F0.imprint","IMPRINT",FACE,{"disambiguationData":[TD([[makeQuery(id+"F0.imprint","IMPRINT",EDGE,{"disambiguationData":[TD([[subQ13,1.0]])],"derivedFrom":subQ12}),-1.0]])]});}
            var Q18;
            {var subQ2=sQuery(id+"F0.wireOp",EDGE,"E203.1.0.147");var subQ9=sQuery(id+"F0.wireOp",EDGE,"E203.1.0.19");var subQ10=makeQuery(id+"F0.imprint","INTERSECT",VERTEX,{"derivedFrom":[subQ9,subQ2]});Q18=makeQuery(id+"F0.imprint","IMPRINT",FACE,{"disambiguationData":[TD([[makeQuery(id+"F0.imprint","IMPRINT",EDGE,{"disambiguationData":[TD([[subQ10,-1.0]])],"derivedFrom":subQ9}),1.0]])]});}
            var Q19;
            {var subQ0=sQuery(id+"F0.wireOp",EDGE,"E59");var subQ1=sQuery(id+"F0.wireOp",EDGE,"E38.MirrorCS");var subQ2=makeQuery(id+"F0.imprint","INTERSECT",VERTEX,{"derivedFrom":[subQ1,subQ0]});Q19=makeQuery(id+"F0.imprint","IMPRINT",FACE,{"disambiguationData":[TD([[makeQuery(id+"F0.imprint","IMPRINT",EDGE,{"disambiguationData":[TD([[subQ2,1.0]])],"derivedFrom":subQ1}),-1.0]])]});}
            var Q20;
            {var subQ1=sQuery(id+"F0.wireOp",EDGE,"E38.MirrorCS");var subQ5=sQuery(id+"F0.wireOp",EDGE,"E57");var subQ12=makeQuery(id+"F0.imprint","INTERSECT",VERTEX,{"derivedFrom":[subQ1,subQ5]});Q20=makeQuery(id+"F0.imprint","IMPRINT",FACE,{"disambiguationData":[TD([[makeQuery(id+"F0.imprint","IMPRINT",EDGE,{"disambiguationData":[TD([[subQ12,-1.0]])],"derivedFrom":subQ1}),-1.0]])]});}
            var Q21;
            {var subQ2=sQuery(id+"F0.wireOp",EDGE,"E203.1.0.183");var subQ8=sQuery(id+"F0.wireOp",EDGE,"E203.1.0.19");var subQ14=makeQuery(id+"F0.imprint","INTERSECT",VERTEX,{"derivedFrom":[subQ8,subQ2]});Q21=makeQuery(id+"F0.imprint","IMPRINT",FACE,{"disambiguationData":[TD([[makeQuery(id+"F0.imprint","IMPRINT",EDGE,{"disambiguationData":[TD([[subQ14,1.0]])],"derivedFrom":subQ8}),1.0]])]});}
            var Q22;
            {var subQ2=sQuery(id+"F0.wireOp",EDGE,"E203.2.0.147");var subQ9=sQuery(id+"F0.wireOp",EDGE,"E203.2.0.19");var subQ10=makeQuery(id+"F0.imprint","INTERSECT",VERTEX,{"derivedFrom":[subQ9,subQ2]});Q22=makeQuery(id+"F0.imprint","IMPRINT",FACE,{"disambiguationData":[TD([[makeQuery(id+"F0.imprint","IMPRINT",EDGE,{"disambiguationData":[TD([[subQ10,-1.0]])],"derivedFrom":subQ9}),1.0]])]});}
            var Q23;
            {var subQ2=sQuery(id+"F0.wireOp",EDGE,"E203.2.0.183");var subQ5=sQuery(id+"F0.wireOp",EDGE,"E203.2.0.19");var subQ14=makeQuery(id+"F0.imprint","INTERSECT",VERTEX,{"derivedFrom":[subQ5,subQ2]});Q23=makeQuery(id+"F0.imprint","IMPRINT",FACE,{"disambiguationData":[TD([[makeQuery(id+"F0.imprint","IMPRINT",EDGE,{"disambiguationData":[TD([[subQ14,1.0]])],"derivedFrom":subQ5}),1.0]])]});}
            var Q24;
            {var subQ0=sQuery(id+"F0.wireOp",EDGE,"E203.2.0.99");var subQ4=sQuery(id+"F0.wireOp",EDGE,"E203.2.0.41");var subQ5=makeQuery(id+"F0.imprint","INTERSECT",VERTEX,{"derivedFrom":[subQ4,subQ0]});Q24=makeQuery(id+"F0.imprint","IMPRINT",FACE,{"disambiguationData":[TD([[makeQuery(id+"F0.imprint","IMPRINT",EDGE,{"disambiguationData":[TD([[subQ5,1.0]])],"derivedFrom":subQ4}),1.0]])]});}
            var Q25;
            {var subQ0=sQuery(id+"F0.wireOp",EDGE,"E203.2.0.137");var subQ1=sQuery(id+"F0.wireOp",EDGE,"E203.2.0.41");var subQ2=makeQuery(id+"F0.imprint","INTERSECT",VERTEX,{"derivedFrom":[subQ1,subQ0]});Q25=makeQuery(id+"F0.imprint","IMPRINT",FACE,{"disambiguationData":[TD([[makeQuery(id+"F0.imprint","IMPRINT",EDGE,{"disambiguationData":[TD([[subQ2,1.0]])],"derivedFrom":subQ1}),1.0]])]});}
            var Q26;
            {var subQ6=sQuery(id+"F0.wireOp",EDGE,"E203.1.0.99");var subQ9=sQuery(id+"F0.wireOp",EDGE,"E203.1.0.41");var subQ13=makeQuery(id+"F0.imprint","INTERSECT",VERTEX,{"derivedFrom":[subQ9,subQ6]});Q26=makeQuery(id+"F0.imprint","IMPRINT",FACE,{"disambiguationData":[TD([[makeQuery(id+"F0.imprint","IMPRINT",EDGE,{"disambiguationData":[TD([[subQ13,1.0]])],"derivedFrom":subQ9}),1.0]])]});}
            var Q27;
            {var subQ0=sQuery(id+"F0.wireOp",EDGE,"E203.1.0.137");var subQ1=sQuery(id+"F0.wireOp",EDGE,"E203.1.0.41");var subQ2=makeQuery(id+"F0.imprint","INTERSECT",VERTEX,{"derivedFrom":[subQ1,subQ0]});Q27=makeQuery(id+"F0.imprint","IMPRINT",FACE,{"disambiguationData":[TD([[makeQuery(id+"F0.imprint","IMPRINT",EDGE,{"disambiguationData":[TD([[subQ2,1.0]])],"derivedFrom":subQ1}),1.0]])]});}
            var Q28;
            {var subQ7=sQuery(id+"F0.wireOp",EDGE,"E52.MirrorCS");var subQ10=sQuery(id+"F0.wireOp",EDGE,"E2.MirrorCS");var subQ14=makeQuery(id+"F0.imprint","INTERSECT",VERTEX,{"derivedFrom":[subQ10,subQ7]});Q28=makeQuery(id+"F0.imprint","IMPRINT",FACE,{"disambiguationData":[TD([[makeQuery(id+"F0.imprint","IMPRINT",EDGE,{"disambiguationData":[TD([[subQ14,-1.0]])],"derivedFrom":subQ10}),1.0]])]});}
            var Q29;
            {var subQ2=sQuery(id+"F0.wireOp",EDGE,"E8.MirrorCS");var subQ4=sQuery(id+"F0.wireOp",EDGE,"E24");var subQ8=makeQuery(id+"F0.imprint","INTERSECT",VERTEX,{"derivedFrom":[subQ2,subQ4]});Q29=makeQuery(id+"F0.imprint","IMPRINT",FACE,{"disambiguationData":[TD([[makeQuery(id+"F0.imprint","IMPRINT",EDGE,{"disambiguationData":[TD([[subQ8,-1.0]])],"derivedFrom":subQ2}),-1.0]])]});}
            extrude(context, id + "F3", {"entities" : qUnion([Q0, Q1, Q2, Q3, Q4, Q5, Q6, Q7, Q8, Q9, Q10, Q11, Q12, Q13, Q14, Q15, Q16, Q17, Q18, Q19, Q20, Q21, Q22, Q23, Q24, Q25, Q26, Q27, Q28, Q29]), "depth" : 8 * mm});
        }
        {
            var Q0;
            {var subQ7=sQuery(id+"F0.wireOp",EDGE,"E162.MirrorCS");Q0=makeQuery(id+"F0.imprint","IMPRINT",FACE,{"disambiguationData":[TD([[makeQuery(id+"F0.imprint","IMPRINT",EDGE,{"derivedFrom":subQ7}),1.0]])]});}
            var Q1;
            {var subQ1=sQuery(id+"F0.wireOp",EDGE,"E203.1.0.31");Q1=makeQuery(id+"F0.imprint","IMPRINT",FACE,{"disambiguationData":[TD([[makeQuery(id+"F0.imprint","IMPRINT",EDGE,{"derivedFrom":subQ1}),-1.0]])]});}
            var Q2;
            {var subQ4=sQuery(id+"F0.wireOp",EDGE,"E203.2.0.31");Q2=makeQuery(id+"F0.imprint","IMPRINT",FACE,{"disambiguationData":[TD([[makeQuery(id+"F0.imprint","IMPRINT",EDGE,{"derivedFrom":subQ4}),-1.0]])]});}
            var Q3;
            {var subQ1=sQuery(id+"F0.wireOp",EDGE,"E203.2.0.13");Q3=makeQuery(id+"F0.imprint","IMPRINT",FACE,{"disambiguationData":[TD([[makeQuery(id+"F0.imprint","IMPRINT",EDGE,{"derivedFrom":subQ1}),-1.0]])]});}
            var Q4;
            {var subQ1=sQuery(id+"F0.wireOp",EDGE,"E203.1.0.13");Q4=makeQuery(id+"F0.imprint","IMPRINT",FACE,{"disambiguationData":[TD([[makeQuery(id+"F0.imprint","IMPRINT",EDGE,{"derivedFrom":subQ1}),-1.0]])]});}
            var Q5;
            {var subQ3=sQuery(id+"F0.wireOp",EDGE,"E200");Q5=makeQuery(id+"F0.imprint","IMPRINT",FACE,{"disambiguationData":[TD([[makeQuery(id+"F0.imprint","IMPRINT",EDGE,{"derivedFrom":subQ3}),-1.0]])]});}
            var Q6;
            {var subQ5=sQuery(id+"F0.wireOp",EDGE,"E76.MirrorCS");Q6=makeQuery(id+"F0.imprint","IMPRINT",FACE,{"disambiguationData":[TD([[makeQuery(id+"F0.imprint","IMPRINT",EDGE,{"derivedFrom":subQ5}),1.0]])]});}
            var Q7;
            {var subQ5=sQuery(id+"F0.wireOp",EDGE,"E203.1.0.53");Q7=makeQuery(id+"F0.imprint","IMPRINT",FACE,{"disambiguationData":[TD([[makeQuery(id+"F0.imprint","IMPRINT",EDGE,{"derivedFrom":subQ5}),-1.0]])]});}
            var Q8;
            {var subQ4=sQuery(id+"F0.wireOp",EDGE,"E203.2.0.53");Q8=makeQuery(id+"F0.imprint","IMPRINT",FACE,{"disambiguationData":[TD([[makeQuery(id+"F0.imprint","IMPRINT",EDGE,{"derivedFrom":subQ4}),-1.0]])]});}
            var Q9;
            {var subQ1=sQuery(id+"F0.wireOp",EDGE,"E203.2.0.5");Q9=makeQuery(id+"F0.imprint","IMPRINT",FACE,{"disambiguationData":[TD([[makeQuery(id+"F0.imprint","IMPRINT",EDGE,{"derivedFrom":subQ1}),-1.0]])]});}
            var Q10;
            {var subQ1=sQuery(id+"F0.wireOp",EDGE,"E203.1.0.5");Q10=makeQuery(id+"F0.imprint","IMPRINT",FACE,{"disambiguationData":[TD([[makeQuery(id+"F0.imprint","IMPRINT",EDGE,{"derivedFrom":subQ1}),-1.0]])]});}
            var Q11;
            {var subQ3=sQuery(id+"F0.wireOp",EDGE,"E199");Q11=makeQuery(id+"F0.imprint","IMPRINT",FACE,{"disambiguationData":[TD([[makeQuery(id+"F0.imprint","IMPRINT",EDGE,{"derivedFrom":subQ3}),-1.0]])]});}
            var Q12;
            {var subQ1=sQuery(id+"F0.wireOp",EDGE,"E22");Q12=makeQuery(id+"F0.imprint","IMPRINT",FACE,{"disambiguationData":[TD([[makeQuery(id+"F0.imprint","IMPRINT",EDGE,{"derivedFrom":subQ1}),1.0]])]});}
            var Q13;
            {var subQ4=sQuery(id+"F0.wireOp",EDGE,"E203.1.0.46");Q13=makeQuery(id+"F0.imprint","IMPRINT",FACE,{"disambiguationData":[TD([[makeQuery(id+"F0.imprint","IMPRINT",EDGE,{"derivedFrom":subQ4}),-1.0]])]});}
            var Q14;
            {var subQ1=sQuery(id+"F0.wireOp",EDGE,"E203.2.0.46");Q14=makeQuery(id+"F0.imprint","IMPRINT",FACE,{"disambiguationData":[TD([[makeQuery(id+"F0.imprint","IMPRINT",EDGE,{"derivedFrom":subQ1}),-1.0]])]});}
            extrude(context, id + "F4", {"entities" : qUnion([Q0, Q1, Q2, Q3, Q4, Q5, Q6, Q7, Q8, Q9, Q10, Q11, Q12, Q13, Q14]), "depth" : 10 * mm});
        }
        {
            var Q0;
            {var subQ0=sQuery(id+"F0.wireOp",EDGE,"E173.MirrorCS");Q0=makeQuery(id+"F0.imprint","IMPRINT",FACE,{"disambiguationData":[TD([[makeQuery(id+"F0.imprint","IMPRINT",EDGE,{"derivedFrom":subQ0}),1.0]])]});}
            var Q1;
            {var subQ0=sQuery(id+"F0.wireOp",EDGE,"E203.1.0.4");Q1=makeQuery(id+"F0.imprint","IMPRINT",FACE,{"disambiguationData":[TD([[makeQuery(id+"F0.imprint","IMPRINT",EDGE,{"derivedFrom":subQ0}),1.0]])]});}
            var Q2;
            {var subQ0=sQuery(id+"F0.wireOp",EDGE,"E203.2.0.4");Q2=makeQuery(id+"F0.imprint","IMPRINT",FACE,{"disambiguationData":[TD([[makeQuery(id+"F0.imprint","IMPRINT",EDGE,{"derivedFrom":subQ0}),1.0]])]});}
            var Q3;
            {var subQ0=sQuery(id+"F0.wireOp",EDGE,"E203.2.0.37");Q3=makeQuery(id+"F0.imprint","IMPRINT",FACE,{"disambiguationData":[TD([[makeQuery(id+"F0.imprint","IMPRINT",EDGE,{"derivedFrom":subQ0}),-1.0]])]});}
            var Q4;
            {var subQ0=sQuery(id+"F0.wireOp",EDGE,"E203.1.0.37");Q4=makeQuery(id+"F0.imprint","IMPRINT",FACE,{"disambiguationData":[TD([[makeQuery(id+"F0.imprint","IMPRINT",EDGE,{"derivedFrom":subQ0}),-1.0]])]});}
            var Q5;
            {var subQ0=sQuery(id+"F0.wireOp",EDGE,"E146.MirrorCS");Q5=makeQuery(id+"F0.imprint","IMPRINT",FACE,{"disambiguationData":[TD([[makeQuery(id+"F0.imprint","IMPRINT",EDGE,{"derivedFrom":subQ0}),-1.0]])]});}
            var Q6;
            {var subQ0=sQuery(id+"F0.wireOp",EDGE,"E116.MirrorCS");Q6=makeQuery(id+"F0.imprint","IMPRINT",FACE,{"disambiguationData":[TD([[makeQuery(id+"F0.imprint","IMPRINT",EDGE,{"derivedFrom":subQ0}),1.0]])]});}
            var Q7;
            {var subQ0=sQuery(id+"F0.wireOp",EDGE,"E203.1.0.20");Q7=makeQuery(id+"F0.imprint","IMPRINT",FACE,{"disambiguationData":[TD([[makeQuery(id+"F0.imprint","IMPRINT",EDGE,{"derivedFrom":subQ0}),1.0]])]});}
            var Q8;
            {var subQ0=sQuery(id+"F0.wireOp",EDGE,"E203.2.0.20");Q8=makeQuery(id+"F0.imprint","IMPRINT",FACE,{"disambiguationData":[TD([[makeQuery(id+"F0.imprint","IMPRINT",EDGE,{"derivedFrom":subQ0}),1.0]])]});}
            var Q9;
            {var subQ0=sQuery(id+"F0.wireOp",EDGE,"E203.2.0.38");Q9=makeQuery(id+"F0.imprint","IMPRINT",FACE,{"disambiguationData":[TD([[makeQuery(id+"F0.imprint","IMPRINT",EDGE,{"derivedFrom":subQ0}),-1.0]])]});}
            var Q10;
            {var subQ0=sQuery(id+"F0.wireOp",EDGE,"E203.1.0.38");Q10=makeQuery(id+"F0.imprint","IMPRINT",FACE,{"disambiguationData":[TD([[makeQuery(id+"F0.imprint","IMPRINT",EDGE,{"derivedFrom":subQ0}),-1.0]])]});}
            var Q11;
            {var subQ0=sQuery(id+"F0.wireOp",EDGE,"E87.MirrorCS");Q11=makeQuery(id+"F0.imprint","IMPRINT",FACE,{"disambiguationData":[TD([[makeQuery(id+"F0.imprint","IMPRINT",EDGE,{"derivedFrom":subQ0}),-1.0]])]});}
            var Q12;
            {var subQ0=sQuery(id+"F0.wireOp",EDGE,"E46.MirrorCS");Q12=makeQuery(id+"F0.imprint","IMPRINT",FACE,{"disambiguationData":[TD([[makeQuery(id+"F0.imprint","IMPRINT",EDGE,{"derivedFrom":subQ0}),1.0]])]});}
            var Q13;
            {var subQ0=sQuery(id+"F0.wireOp",EDGE,"E203.1.0.11");Q13=makeQuery(id+"F0.imprint","IMPRINT",FACE,{"disambiguationData":[TD([[makeQuery(id+"F0.imprint","IMPRINT",EDGE,{"derivedFrom":subQ0}),1.0]])]});}
            var Q14;
            {var subQ0=sQuery(id+"F0.wireOp",EDGE,"E203.2.0.11");Q14=makeQuery(id+"F0.imprint","IMPRINT",FACE,{"disambiguationData":[TD([[makeQuery(id+"F0.imprint","IMPRINT",EDGE,{"derivedFrom":subQ0}),1.0]])]});}
            var Q15;
            {var subQ0=sQuery(id+"F0.wireOp",EDGE,"E203.2.0.27");Q15=makeQuery(id+"F0.imprint","IMPRINT",FACE,{"disambiguationData":[TD([[makeQuery(id+"F0.imprint","IMPRINT",EDGE,{"derivedFrom":subQ0}),-1.0]])]});}
            var Q16;
            {var subQ0=sQuery(id+"F0.wireOp",EDGE,"E203.1.0.27");Q16=makeQuery(id+"F0.imprint","IMPRINT",FACE,{"disambiguationData":[TD([[makeQuery(id+"F0.imprint","IMPRINT",EDGE,{"derivedFrom":subQ0}),-1.0]])]});}
            var Q17;
            {var subQ0=sQuery(id+"F0.wireOp",EDGE,"E12.MirrorCS");Q17=makeQuery(id+"F0.imprint","IMPRINT",FACE,{"disambiguationData":[TD([[makeQuery(id+"F0.imprint","IMPRINT",EDGE,{"derivedFrom":subQ0}),-1.0]])]});}
            extrude(context, id + "F5", {"entities" : qUnion([Q0, Q1, Q2, Q3, Q4, Q5, Q6, Q7, Q8, Q9, Q10, Q11, Q12, Q13, Q14, Q15, Q16, Q17]), "depth" : 8 * mm});
        }
        {
            var Q0;
            {var subQ2=sQuery(id+"F0.wireOp",EDGE,"E166.MirrorCS");Q0=makeQuery(id+"F0.imprint","IMPRINT",FACE,{"disambiguationData":[TD([[makeQuery(id+"F0.imprint","IMPRINT",EDGE,{"derivedFrom":subQ2}),1.0]])]});}
            var Q1;
            {var subQ2=sQuery(id+"F0.wireOp",EDGE,"E163.MirrorCS");Q1=makeQuery(id+"F0.imprint","IMPRINT",FACE,{"disambiguationData":[TD([[makeQuery(id+"F0.imprint","IMPRINT",EDGE,{"derivedFrom":subQ2}),1.0]])]});}
            var Q2;
            {var subQ4=sQuery(id+"F0.wireOp",EDGE,"E203.1.0.4");Q2=makeQuery(id+"F0.imprint","IMPRINT",FACE,{"disambiguationData":[TD([[makeQuery(id+"F0.imprint","IMPRINT",EDGE,{"derivedFrom":subQ4}),-1.0]])]});}
            var Q3;
            {var subQ0=sQuery(id+"F0.wireOp",EDGE,"E203.1.0.56");Q3=makeQuery(id+"F0.imprint","IMPRINT",FACE,{"disambiguationData":[TD([[makeQuery(id+"F0.imprint","IMPRINT",EDGE,{"derivedFrom":subQ0}),-1.0]])]});}
            var Q4;
            {var subQ4=sQuery(id+"F0.wireOp",EDGE,"E203.2.0.4");Q4=makeQuery(id+"F0.imprint","IMPRINT",FACE,{"disambiguationData":[TD([[makeQuery(id+"F0.imprint","IMPRINT",EDGE,{"derivedFrom":subQ4}),-1.0]])]});}
            var Q5;
            {var subQ0=sQuery(id+"F0.wireOp",EDGE,"E203.2.0.56");Q5=makeQuery(id+"F0.imprint","IMPRINT",FACE,{"disambiguationData":[TD([[makeQuery(id+"F0.imprint","IMPRINT",EDGE,{"derivedFrom":subQ0}),-1.0]])]});}
            var Q6;
            {var subQ3=sQuery(id+"F0.wireOp",EDGE,"E203.2.0.47");Q6=makeQuery(id+"F0.imprint","IMPRINT",FACE,{"disambiguationData":[TD([[makeQuery(id+"F0.imprint","IMPRINT",EDGE,{"derivedFrom":subQ3}),1.0]])]});}
            var Q7;
            {var subQ0=sQuery(id+"F0.wireOp",EDGE,"E203.2.0.37");Q7=makeQuery(id+"F0.imprint","IMPRINT",FACE,{"disambiguationData":[TD([[makeQuery(id+"F0.imprint","IMPRINT",EDGE,{"derivedFrom":subQ0}),1.0]])]});}
            var Q8;
            {var subQ3=sQuery(id+"F0.wireOp",EDGE,"E203.1.0.47");Q8=makeQuery(id+"F0.imprint","IMPRINT",FACE,{"disambiguationData":[TD([[makeQuery(id+"F0.imprint","IMPRINT",EDGE,{"derivedFrom":subQ3}),1.0]])]});}
            var Q9;
            {var subQ0=sQuery(id+"F0.wireOp",EDGE,"E203.1.0.37");Q9=makeQuery(id+"F0.imprint","IMPRINT",FACE,{"disambiguationData":[TD([[makeQuery(id+"F0.imprint","IMPRINT",EDGE,{"derivedFrom":subQ0}),1.0]])]});}
            var Q10;
            {var subQ4=sQuery(id+"F0.wireOp",EDGE,"E129.MirrorCS");Q10=makeQuery(id+"F0.imprint","IMPRINT",FACE,{"disambiguationData":[TD([[makeQuery(id+"F0.imprint","IMPRINT",EDGE,{"derivedFrom":subQ4}),-1.0]])]});}
            var Q11;
            {var subQ5=sQuery(id+"F0.wireOp",EDGE,"E136.MirrorCS");Q11=makeQuery(id+"F0.imprint","IMPRINT",FACE,{"disambiguationData":[TD([[makeQuery(id+"F0.imprint","IMPRINT",EDGE,{"derivedFrom":subQ5}),-1.0]])]});}
            var Q12;
            {var subQ5=sQuery(id+"F0.wireOp",EDGE,"E96.MirrorCS");Q12=makeQuery(id+"F0.imprint","IMPRINT",FACE,{"disambiguationData":[TD([[makeQuery(id+"F0.imprint","IMPRINT",EDGE,{"derivedFrom":subQ5}),1.0]])]});}
            var Q13;
            {var subQ7=sQuery(id+"F0.wireOp",EDGE,"E97.MirrorCS");Q13=makeQuery(id+"F0.imprint","IMPRINT",FACE,{"disambiguationData":[TD([[makeQuery(id+"F0.imprint","IMPRINT",EDGE,{"derivedFrom":subQ7}),1.0]])]});}
            var Q14;
            {var subQ4=sQuery(id+"F0.wireOp",EDGE,"E203.1.0.61");Q14=makeQuery(id+"F0.imprint","IMPRINT",FACE,{"disambiguationData":[TD([[makeQuery(id+"F0.imprint","IMPRINT",EDGE,{"derivedFrom":subQ4}),-1.0]])]});}
            var Q15;
            {var subQ1=sQuery(id+"F0.wireOp",EDGE,"E203.1.0.20");Q15=makeQuery(id+"F0.imprint","IMPRINT",FACE,{"disambiguationData":[TD([[makeQuery(id+"F0.imprint","IMPRINT",EDGE,{"derivedFrom":subQ1}),-1.0]])]});}
            var Q16;
            {var subQ0=sQuery(id+"F0.wireOp",EDGE,"E203.2.0.61");Q16=makeQuery(id+"F0.imprint","IMPRINT",FACE,{"disambiguationData":[TD([[makeQuery(id+"F0.imprint","IMPRINT",EDGE,{"derivedFrom":subQ0}),-1.0]])]});}
            var Q17;
            {var subQ3=sQuery(id+"F0.wireOp",EDGE,"E203.2.0.20");Q17=makeQuery(id+"F0.imprint","IMPRINT",FACE,{"disambiguationData":[TD([[makeQuery(id+"F0.imprint","IMPRINT",EDGE,{"derivedFrom":subQ3}),-1.0]])]});}
            var Q18;
            {var subQ3=sQuery(id+"F0.wireOp",EDGE,"E203.2.0.38");Q18=makeQuery(id+"F0.imprint","IMPRINT",FACE,{"disambiguationData":[TD([[makeQuery(id+"F0.imprint","IMPRINT",EDGE,{"derivedFrom":subQ3}),1.0]])]});}
            var Q19;
            {var subQ3=sQuery(id+"F0.wireOp",EDGE,"E203.2.0.54");Q19=makeQuery(id+"F0.imprint","IMPRINT",FACE,{"disambiguationData":[TD([[makeQuery(id+"F0.imprint","IMPRINT",EDGE,{"derivedFrom":subQ3}),1.0]])]});}
            var Q20;
            {var subQ3=sQuery(id+"F0.wireOp",EDGE,"E203.1.0.38");Q20=makeQuery(id+"F0.imprint","IMPRINT",FACE,{"disambiguationData":[TD([[makeQuery(id+"F0.imprint","IMPRINT",EDGE,{"derivedFrom":subQ3}),1.0]])]});}
            var Q21;
            {var subQ3=sQuery(id+"F0.wireOp",EDGE,"E203.1.0.54");Q21=makeQuery(id+"F0.imprint","IMPRINT",FACE,{"disambiguationData":[TD([[makeQuery(id+"F0.imprint","IMPRINT",EDGE,{"derivedFrom":subQ3}),1.0]])]});}
            var Q22;
            Q22=makeQuery(id+"F0.imprint","IMPRINT",FACE,{"disambiguationData":[TD([[makeQuery(id+"F0.imprint","IMPRINT",EDGE,{"derivedFrom":sQuery(id+"F0.wireOp",EDGE,"E71.MirrorCS")}),-1.0]])]});
            var Q23;
            Q23=makeQuery(id+"F0.imprint","IMPRINT",FACE,{"disambiguationData":[TD([[makeQuery(id+"F0.imprint","IMPRINT",EDGE,{"derivedFrom":sQuery(id+"F0.wireOp",EDGE,"E61.MirrorCS")}),1.0]])]});
            var Q24;
            {var subQ3=sQuery(id+"F0.wireOp",EDGE,"E27.MirrorCS");Q24=makeQuery(id+"F0.imprint","IMPRINT",FACE,{"disambiguationData":[TD([[makeQuery(id+"F0.imprint","IMPRINT",EDGE,{"derivedFrom":subQ3}),1.0]])]});}
            var Q25;
            Q25=makeQuery(id+"F0.imprint","IMPRINT",FACE,{"disambiguationData":[TD([[makeQuery(id+"F0.imprint","IMPRINT",EDGE,{"derivedFrom":sQuery(id+"F0.wireOp",EDGE,"E32.MirrorCS")}),1.0]])]});
            var Q26;
            {var subQ4=sQuery(id+"F0.wireOp",EDGE,"E203.1.0.11");Q26=makeQuery(id+"F0.imprint","IMPRINT",FACE,{"disambiguationData":[TD([[makeQuery(id+"F0.imprint","IMPRINT",EDGE,{"derivedFrom":subQ4}),-1.0]])]});}
            var Q27;
            {var subQ0=sQuery(id+"F0.wireOp",EDGE,"E203.1.0.55");Q27=makeQuery(id+"F0.imprint","IMPRINT",FACE,{"disambiguationData":[TD([[makeQuery(id+"F0.imprint","IMPRINT",EDGE,{"derivedFrom":subQ0}),-1.0]])]});}
            var Q28;
            {var subQ7=sQuery(id+"F0.wireOp",EDGE,"E203.2.0.11");Q28=makeQuery(id+"F0.imprint","IMPRINT",FACE,{"disambiguationData":[TD([[makeQuery(id+"F0.imprint","IMPRINT",EDGE,{"derivedFrom":subQ7}),-1.0]])]});}
            var Q29;
            {var subQ0=sQuery(id+"F0.wireOp",EDGE,"E203.2.0.55");Q29=makeQuery(id+"F0.imprint","IMPRINT",FACE,{"disambiguationData":[TD([[makeQuery(id+"F0.imprint","IMPRINT",EDGE,{"derivedFrom":subQ0}),-1.0]])]});}
            var Q30;
            {var subQ1=sQuery(id+"F0.wireOp",EDGE,"E203.2.0.27");Q30=makeQuery(id+"F0.imprint","IMPRINT",FACE,{"disambiguationData":[TD([[makeQuery(id+"F0.imprint","IMPRINT",EDGE,{"derivedFrom":subQ1}),1.0]])]});}
            var Q31;
            {var subQ2=sQuery(id+"F0.wireOp",EDGE,"E203.2.0.78");Q31=makeQuery(id+"F0.imprint","IMPRINT",FACE,{"disambiguationData":[TD([[makeQuery(id+"F0.imprint","IMPRINT",EDGE,{"derivedFrom":subQ2}),1.0]])]});}
            var Q32;
            {var subQ1=sQuery(id+"F0.wireOp",EDGE,"E203.1.0.27");Q32=makeQuery(id+"F0.imprint","IMPRINT",FACE,{"disambiguationData":[TD([[makeQuery(id+"F0.imprint","IMPRINT",EDGE,{"derivedFrom":subQ1}),1.0]])]});}
            var Q33;
            {var subQ2=sQuery(id+"F0.wireOp",EDGE,"E203.1.0.78");Q33=makeQuery(id+"F0.imprint","IMPRINT",FACE,{"disambiguationData":[TD([[makeQuery(id+"F0.imprint","IMPRINT",EDGE,{"derivedFrom":subQ2}),1.0]])]});}
            var Q34;
            {var subQ1=sQuery(id+"F0.wireOp",EDGE,"E1.MirrorCS");Q34=makeQuery(id+"F0.imprint","IMPRINT",FACE,{"disambiguationData":[TD([[makeQuery(id+"F0.imprint","IMPRINT",EDGE,{"derivedFrom":subQ1}),-1.0]])]});}
            var Q35;
            {var subQ6=sQuery(id+"F0.wireOp",EDGE,"E5.MirrorCS");Q35=makeQuery(id+"F0.imprint","IMPRINT",FACE,{"disambiguationData":[TD([[makeQuery(id+"F0.imprint","IMPRINT",EDGE,{"derivedFrom":subQ6}),-1.0]])]});}
            extrude(context, id + "F6", {"entities" : qUnion([Q0, Q1, Q2, Q3, Q4, Q5, Q6, Q7, Q8, Q9, Q10, Q11, Q12, Q13, Q14, Q15, Q16, Q17, Q18, Q19, Q20, Q21, Q22, Q23, Q24, Q25, Q26, Q27, Q28, Q29, Q30, Q31, Q32, Q33, Q34, Q35]), "depth" : 5 * mm});
        }
    });
